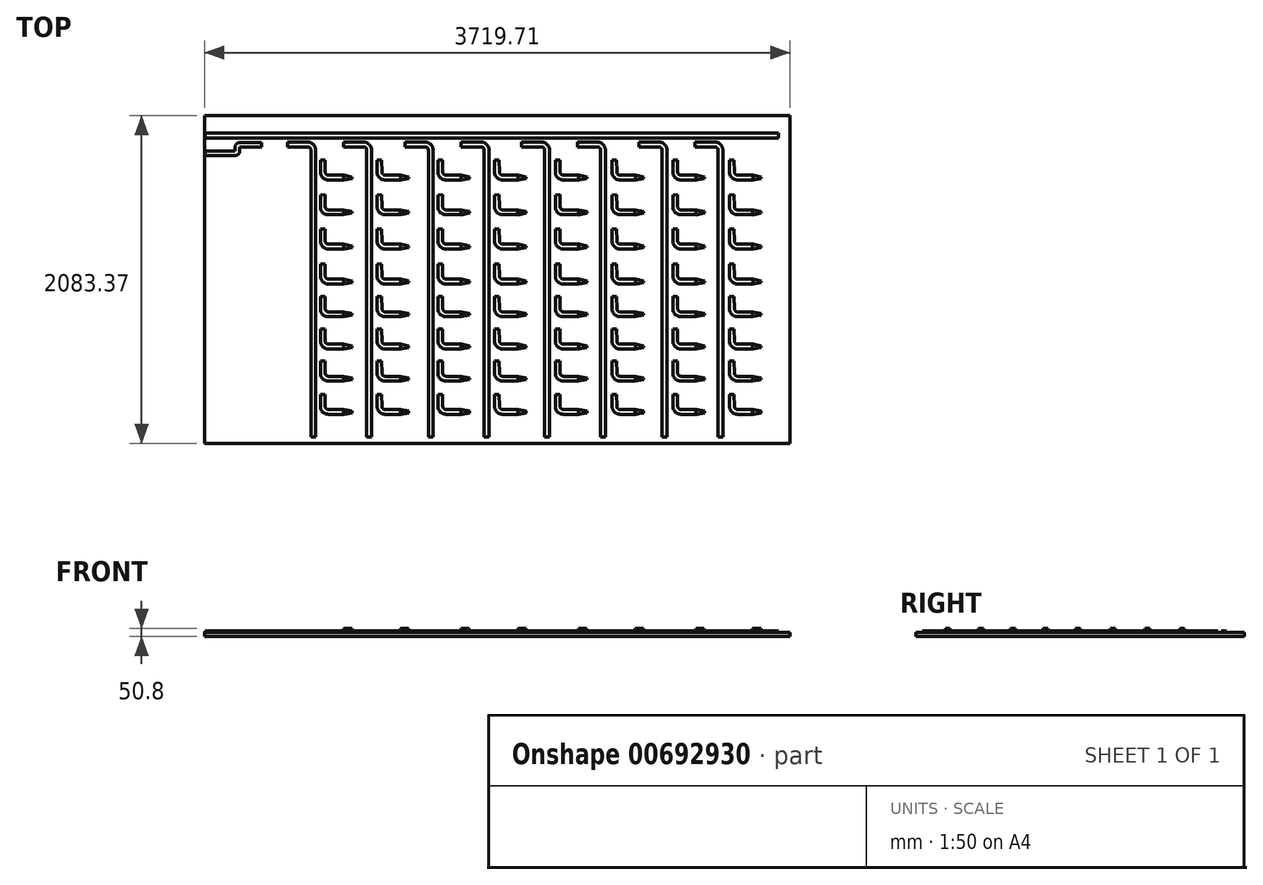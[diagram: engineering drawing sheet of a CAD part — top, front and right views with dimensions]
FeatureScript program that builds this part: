
annotation { "Feature Type Name" : "Feature", "Feature Type Description" : "" }
export const myFeature = defineFeature(function(context is Context, id is Id, definition is map)
    precondition{}
    {
        {
            var Q0;
            Q0=qCreatedBy(makeId("Top.planeOp"),FACE);
            var sketch = newSketch(context, id + "F0", { "sketchPlane" : qUnion([Q0])});
            skLineSegment(sketch, "E0.left", {"start": v(-935.56, 1469.09) * mm, "end": v(-935.56, -614.28) * mm});
            skPoint(sketch, "E0.middle", {"position": v(0, 0) * mm});
            skLineSegment(sketch, "E1", {"start": v(-935.56, 1469.09) * mm, "end": v(2784.15, 1469.09) * mm});
            skLineSegment(sketch, "E2", {"start": v(2784.15, 1469.09) * mm, "end": v(2784.15, -614.28) * mm});
            skLineSegment(sketch, "E3", {"start": v(2784.15, -614.28) * mm, "end": v(-935.56, -614.28) * mm});
            skSolve(sketch);
        }
        {
            var Q0;
            Q0=qSketchRegion(id+"F0",true);
            var Q1;
            Q1=makeQuery(id+"F0.imprint","IMPRINT",FACE,{"disambiguationData":[TD([[makeQuery(id+"F0.imprint","IMPRINT",EDGE,{"derivedFrom":sQuery(id+"F0.wireOp",EDGE,"E0.bottom")}),-1.0]])]});
            extrude(context, id + "F1", {"entities" : qUnion([Q0, Q1]), "oppositeDirection" : true, "depth" : 25.4 * mm, "offsetDistance" : 25.4 * mm});
        }
        {
            var Q0;
            Q0=makeQuery(id+"F1.opExtrude","CAP_FACE",FACE,{"disambiguationData":[OSD([sQuery(id+"F0.wireOp",EDGE,"E0.bottom"),sQuery(id+"F0.wireOp",EDGE,"E0.top"),sQuery(id+"F0.wireOp",EDGE,"E0.left"),sQuery(id+"F0.wireOp",EDGE,"E0.right")])],"isStart":true});
            var sketch = newSketch(context, id + "F2", { "sketchPlane" : qUnion([Q0])});
            skLineSegment(sketch, "E4", {"start": v(-51.41, 16.02) * mm, "end": v(0, 4.87) * mm});
            skLineSegment(sketch, "E5", {"start": v(0, 4.87) * mm, "end": v(0, -4.87) * mm});
            skLineSegment(sketch, "E6", {"start": v(0, -4.87) * mm, "end": v(-51.41, -14.6) * mm});
            skLineSegment(sketch, "E7", {"start": v(-51.41, 16.02) * mm, "end": v(-149.21, 16.02) * mm});
            skLineSegment(sketch, "E8", {"start": v(-149.21, -14.6) * mm, "end": v(-51.41, -14.6) * mm});
            skArc(sketch, "E9", {"start": v(-149.21, 16.02) * mm, "mid": v(-163.12, 21.71) * mm, "end": v(-169.05, 35.52) * mm});
            skArc(sketch, "E10", {"start": v(-149.21, -14.6) * mm, "mid": v(-184.84, 0.05) * mm, "end": v(-199.87, 35.52) * mm});
            skLineSegment(sketch, "E11", {"start": v(-169.05, 35.52) * mm, "end": v(-170.37, 112.54) * mm});
            skLineSegment(sketch, "E12", {"start": v(-170.37, 112.54) * mm, "end": v(-199.87, 112.03) * mm});
            skLineSegment(sketch, "E13", {"start": v(-199.87, 112.03) * mm, "end": v(-199.87, 35.52) * mm});
            skLineSegment(sketch, "E14", {"start": v(-51.41, 221.54) * mm, "end": v(0, 210.39) * mm});
            skLineSegment(sketch, "E15", {"start": v(0, 210.39) * mm, "end": v(0, 200.65) * mm});
            skLineSegment(sketch, "E16", {"start": v(0, 200.65) * mm, "end": v(-51.41, 190.92) * mm});
            skLineSegment(sketch, "E17", {"start": v(-51.41, 221.54) * mm, "end": v(-149.21, 221.54) * mm});
            skLineSegment(sketch, "E18", {"start": v(-149.21, 190.92) * mm, "end": v(-51.41, 190.92) * mm});
            skArc(sketch, "E19", {"start": v(-149.21, 221.54) * mm, "mid": v(-163.12, 227.23) * mm, "end": v(-169.05, 241.04) * mm});
            skArc(sketch, "E20", {"start": v(-149.21, 190.92) * mm, "mid": v(-184.84, 205.56) * mm, "end": v(-199.87, 241.04) * mm});
            skLineSegment(sketch, "E21", {"start": v(-169.05, 241.04) * mm, "end": v(-170.37, 318.06) * mm});
            skLineSegment(sketch, "E22", {"start": v(-170.37, 318.06) * mm, "end": v(-199.87, 317.55) * mm});
            skLineSegment(sketch, "E23", {"start": v(-199.87, 317.55) * mm, "end": v(-199.87, 241.04) * mm});
            skLineSegment(sketch, "E24", {"start": v(-51.41, -187.5) * mm, "end": v(0, -198.65) * mm});
            skLineSegment(sketch, "E25", {"start": v(0, -198.65) * mm, "end": v(0, -208.39) * mm});
            skLineSegment(sketch, "E26", {"start": v(0, -208.39) * mm, "end": v(-51.41, -218.12) * mm});
            skLineSegment(sketch, "E27", {"start": v(-51.41, -187.5) * mm, "end": v(-149.21, -187.5) * mm});
            skLineSegment(sketch, "E28", {"start": v(-149.21, -218.12) * mm, "end": v(-51.41, -218.12) * mm});
            skArc(sketch, "E29", {"start": v(-149.21, -187.5) * mm, "mid": v(-163.12, -181.8) * mm, "end": v(-169.05, -168) * mm});
            skArc(sketch, "E30", {"start": v(-149.21, -218.12) * mm, "mid": v(-184.84, -203.48) * mm, "end": v(-199.87, -168) * mm});
            skLineSegment(sketch, "E31", {"start": v(-169.05, -168) * mm, "end": v(-170.37, -90.98) * mm});
            skLineSegment(sketch, "E32", {"start": v(-170.37, -90.98) * mm, "end": v(-199.87, -91.49) * mm});
            skLineSegment(sketch, "E33", {"start": v(-199.87, -91.49) * mm, "end": v(-199.87, -168) * mm});
            skLineSegment(sketch, "E34", {"start": v(-51.41, -398.32) * mm, "end": v(0, -409.47) * mm});
            skLineSegment(sketch, "E35", {"start": v(0, -409.47) * mm, "end": v(0, -419.2) * mm});
            skLineSegment(sketch, "E36", {"start": v(0, -419.2) * mm, "end": v(-51.41, -428.94) * mm});
            skLineSegment(sketch, "E37", {"start": v(-51.41, -398.32) * mm, "end": v(-149.21, -398.32) * mm});
            skLineSegment(sketch, "E38", {"start": v(-149.21, -428.94) * mm, "end": v(-51.41, -428.94) * mm});
            skArc(sketch, "E39", {"start": v(-149.21, -398.32) * mm, "mid": v(-163.12, -392.63) * mm, "end": v(-169.05, -378.82) * mm});
            skArc(sketch, "E40", {"start": v(-149.21, -428.94) * mm, "mid": v(-184.84, -414.3) * mm, "end": v(-199.87, -378.82) * mm});
            skLineSegment(sketch, "E41", {"start": v(-169.05, -378.82) * mm, "end": v(-170.37, -301.8) * mm});
            skLineSegment(sketch, "E42", {"start": v(-170.37, -301.8) * mm, "end": v(-199.87, -302.3) * mm});
            skLineSegment(sketch, "E43", {"start": v(-199.87, -302.3) * mm, "end": v(-199.87, -378.82) * mm});
            skLineSegment(sketch, "E44", {"start": v(-51.41, 429.24) * mm, "end": v(0, 418.08) * mm});
            skLineSegment(sketch, "E45", {"start": v(0, 418.08) * mm, "end": v(0, 408.35) * mm});
            skLineSegment(sketch, "E46", {"start": v(0, 408.35) * mm, "end": v(-51.41, 398.61) * mm});
            skLineSegment(sketch, "E47", {"start": v(-51.41, 429.24) * mm, "end": v(-149.21, 429.24) * mm});
            skLineSegment(sketch, "E48", {"start": v(-149.21, 398.61) * mm, "end": v(-51.41, 398.61) * mm});
            skArc(sketch, "E49", {"start": v(-149.21, 429.24) * mm, "mid": v(-163.12, 434.93) * mm, "end": v(-169.05, 448.73) * mm});
            skArc(sketch, "E50", {"start": v(-149.21, 398.61) * mm, "mid": v(-184.84, 413.26) * mm, "end": v(-199.87, 448.73) * mm});
            skLineSegment(sketch, "E51", {"start": v(-169.05, 448.73) * mm, "end": v(-170.37, 525.76) * mm});
            skLineSegment(sketch, "E52", {"start": v(-170.37, 525.76) * mm, "end": v(-199.87, 525.25) * mm});
            skLineSegment(sketch, "E53", {"start": v(-199.87, 525.25) * mm, "end": v(-199.87, 448.73) * mm});
            skLineSegment(sketch, "E54", {"start": v(-51.41, 651.7) * mm, "end": v(0, 640.54) * mm});
            skLineSegment(sketch, "E55", {"start": v(0, 640.54) * mm, "end": v(0, 630.8) * mm});
            skLineSegment(sketch, "E56", {"start": v(0, 630.8) * mm, "end": v(-51.41, 621.07) * mm});
            skLineSegment(sketch, "E57", {"start": v(-51.41, 651.7) * mm, "end": v(-149.21, 651.7) * mm});
            skLineSegment(sketch, "E58", {"start": v(-149.21, 621.07) * mm, "end": v(-51.41, 621.07) * mm});
            skArc(sketch, "E59", {"start": v(-149.21, 651.7) * mm, "mid": v(-163.12, 657.39) * mm, "end": v(-169.05, 671.2) * mm});
            skArc(sketch, "E60", {"start": v(-149.21, 621.07) * mm, "mid": v(-184.84, 635.72) * mm, "end": v(-199.87, 671.2) * mm});
            skLineSegment(sketch, "E61", {"start": v(-169.05, 671.2) * mm, "end": v(-170.37, 748.22) * mm});
            skLineSegment(sketch, "E62", {"start": v(-170.37, 748.22) * mm, "end": v(-199.87, 747.71) * mm});
            skLineSegment(sketch, "E63", {"start": v(-199.87, 747.71) * mm, "end": v(-199.87, 671.2) * mm});
            skLineSegment(sketch, "E64", {"start": v(-51.41, 869.02) * mm, "end": v(0, 857.87) * mm});
            skLineSegment(sketch, "E65", {"start": v(0, 857.87) * mm, "end": v(0, 848.13) * mm});
            skLineSegment(sketch, "E66", {"start": v(0, 848.13) * mm, "end": v(-51.41, 838.4) * mm});
            skLineSegment(sketch, "E67", {"start": v(-51.41, 869.02) * mm, "end": v(-149.21, 869.02) * mm});
            skLineSegment(sketch, "E68", {"start": v(-149.21, 838.4) * mm, "end": v(-51.41, 838.4) * mm});
            skArc(sketch, "E69", {"start": v(-149.21, 869.02) * mm, "mid": v(-163.12, 874.71) * mm, "end": v(-169.05, 888.52) * mm});
            skArc(sketch, "E70", {"start": v(-149.21, 838.4) * mm, "mid": v(-184.84, 853.05) * mm, "end": v(-199.87, 888.52) * mm});
            skLineSegment(sketch, "E71", {"start": v(-169.05, 888.52) * mm, "end": v(-170.37, 965.54) * mm});
            skLineSegment(sketch, "E72", {"start": v(-170.37, 965.54) * mm, "end": v(-199.87, 965.04) * mm});
            skLineSegment(sketch, "E73", {"start": v(-199.87, 965.04) * mm, "end": v(-199.87, 888.52) * mm});
            skLineSegment(sketch, "E74", {"start": v(-51.41, 1090.15) * mm, "end": v(0, 1079) * mm});
            skLineSegment(sketch, "E75", {"start": v(0, 1079) * mm, "end": v(0, 1069.26) * mm});
            skLineSegment(sketch, "E76", {"start": v(0, 1069.26) * mm, "end": v(-51.41, 1059.52) * mm});
            skLineSegment(sketch, "E77", {"start": v(-51.41, 1090.15) * mm, "end": v(-149.21, 1090.15) * mm});
            skLineSegment(sketch, "E78", {"start": v(-149.21, 1059.52) * mm, "end": v(-51.41, 1059.52) * mm});
            skArc(sketch, "E79", {"start": v(-149.21, 1090.15) * mm, "mid": v(-163.12, 1095.84) * mm, "end": v(-169.05, 1109.64) * mm});
            skArc(sketch, "E80", {"start": v(-149.21, 1059.52) * mm, "mid": v(-184.84, 1074.17) * mm, "end": v(-199.87, 1109.64) * mm});
            skLineSegment(sketch, "E81", {"start": v(-169.05, 1109.64) * mm, "end": v(-170.37, 1186.67) * mm});
            skLineSegment(sketch, "E82", {"start": v(-170.37, 1186.67) * mm, "end": v(-199.87, 1186.16) * mm});
            skLineSegment(sketch, "E83", {"start": v(-199.87, 1186.16) * mm, "end": v(-199.87, 1109.64) * mm});
            skLineSegment(sketch, "E84", {"start": v(308.62, 16.02) * mm, "end": v(360.03, 4.87) * mm});
            skLineSegment(sketch, "E85", {"start": v(360.03, 4.87) * mm, "end": v(360.03, -4.87) * mm});
            skLineSegment(sketch, "E86", {"start": v(360.03, -4.87) * mm, "end": v(308.62, -14.6) * mm});
            skLineSegment(sketch, "E87", {"start": v(308.62, 16.02) * mm, "end": v(210.82, 16.02) * mm});
            skLineSegment(sketch, "E88", {"start": v(210.82, -14.6) * mm, "end": v(308.62, -14.6) * mm});
            skArc(sketch, "E89", {"start": v(210.82, 16.02) * mm, "mid": v(196.91, 21.71) * mm, "end": v(190.99, 35.52) * mm});
            skArc(sketch, "E90", {"start": v(210.82, -14.6) * mm, "mid": v(175.19, 0.05) * mm, "end": v(160.16, 35.52) * mm});
            skLineSegment(sketch, "E91", {"start": v(190.99, 35.52) * mm, "end": v(189.66, 112.54) * mm});
            skLineSegment(sketch, "E92", {"start": v(189.66, 112.54) * mm, "end": v(160.16, 112.03) * mm});
            skLineSegment(sketch, "E93", {"start": v(160.16, 112.03) * mm, "end": v(160.16, 35.52) * mm});
            skLineSegment(sketch, "E94", {"start": v(308.62, 221.54) * mm, "end": v(360.03, 210.39) * mm});
            skLineSegment(sketch, "E95", {"start": v(360.03, 210.39) * mm, "end": v(360.03, 200.65) * mm});
            skLineSegment(sketch, "E96", {"start": v(360.03, 200.65) * mm, "end": v(308.62, 190.92) * mm});
            skLineSegment(sketch, "E97", {"start": v(308.62, 221.54) * mm, "end": v(210.82, 221.54) * mm});
            skLineSegment(sketch, "E98", {"start": v(210.82, 190.92) * mm, "end": v(308.62, 190.92) * mm});
            skArc(sketch, "E99", {"start": v(210.82, 221.54) * mm, "mid": v(196.91, 227.23) * mm, "end": v(190.99, 241.04) * mm});
            skArc(sketch, "E100", {"start": v(210.82, 190.92) * mm, "mid": v(175.19, 205.56) * mm, "end": v(160.16, 241.04) * mm});
            skLineSegment(sketch, "E101", {"start": v(190.99, 241.04) * mm, "end": v(189.66, 318.06) * mm});
            skLineSegment(sketch, "E102", {"start": v(189.66, 318.06) * mm, "end": v(160.16, 317.55) * mm});
            skLineSegment(sketch, "E103", {"start": v(160.16, 317.55) * mm, "end": v(160.16, 241.04) * mm});
            skLineSegment(sketch, "E104", {"start": v(308.62, -187.5) * mm, "end": v(360.03, -198.65) * mm});
            skLineSegment(sketch, "E105", {"start": v(360.03, -198.65) * mm, "end": v(360.03, -208.39) * mm});
            skLineSegment(sketch, "E106", {"start": v(360.03, -208.39) * mm, "end": v(308.62, -218.12) * mm});
            skLineSegment(sketch, "E107", {"start": v(308.62, -187.5) * mm, "end": v(210.82, -187.5) * mm});
            skLineSegment(sketch, "E108", {"start": v(210.82, -218.12) * mm, "end": v(308.62, -218.12) * mm});
            skArc(sketch, "E109", {"start": v(210.82, -187.5) * mm, "mid": v(196.91, -181.8) * mm, "end": v(190.99, -168) * mm});
            skArc(sketch, "E110", {"start": v(210.82, -218.12) * mm, "mid": v(175.19, -203.48) * mm, "end": v(160.16, -168) * mm});
            skLineSegment(sketch, "E111", {"start": v(190.99, -168) * mm, "end": v(189.66, -90.98) * mm});
            skLineSegment(sketch, "E112", {"start": v(189.66, -90.98) * mm, "end": v(160.16, -91.49) * mm});
            skLineSegment(sketch, "E113", {"start": v(160.16, -91.49) * mm, "end": v(160.16, -168) * mm});
            skLineSegment(sketch, "E114", {"start": v(308.62, -398.32) * mm, "end": v(360.03, -409.47) * mm});
            skLineSegment(sketch, "E115", {"start": v(360.03, -409.47) * mm, "end": v(360.03, -419.2) * mm});
            skLineSegment(sketch, "E116", {"start": v(360.03, -419.2) * mm, "end": v(308.62, -428.94) * mm});
            skLineSegment(sketch, "E117", {"start": v(308.62, -398.32) * mm, "end": v(210.82, -398.32) * mm});
            skLineSegment(sketch, "E118", {"start": v(210.82, -428.94) * mm, "end": v(308.62, -428.94) * mm});
            skArc(sketch, "E119", {"start": v(210.82, -398.32) * mm, "mid": v(196.91, -392.63) * mm, "end": v(190.99, -378.82) * mm});
            skArc(sketch, "E120", {"start": v(210.82, -428.94) * mm, "mid": v(175.19, -414.3) * mm, "end": v(160.16, -378.82) * mm});
            skLineSegment(sketch, "E121", {"start": v(190.99, -378.82) * mm, "end": v(189.66, -301.8) * mm});
            skLineSegment(sketch, "E122", {"start": v(189.66, -301.8) * mm, "end": v(160.16, -302.3) * mm});
            skLineSegment(sketch, "E123", {"start": v(160.16, -302.3) * mm, "end": v(160.16, -378.82) * mm});
            skLineSegment(sketch, "E124", {"start": v(308.62, 429.24) * mm, "end": v(360.03, 418.08) * mm});
            skLineSegment(sketch, "E125", {"start": v(360.03, 418.08) * mm, "end": v(360.03, 408.35) * mm});
            skLineSegment(sketch, "E126", {"start": v(360.03, 408.35) * mm, "end": v(308.62, 398.61) * mm});
            skLineSegment(sketch, "E127", {"start": v(308.62, 429.24) * mm, "end": v(210.82, 429.24) * mm});
            skLineSegment(sketch, "E128", {"start": v(210.82, 398.61) * mm, "end": v(308.62, 398.61) * mm});
            skArc(sketch, "E129", {"start": v(210.82, 429.24) * mm, "mid": v(196.91, 434.93) * mm, "end": v(190.99, 448.73) * mm});
            skArc(sketch, "E130", {"start": v(210.82, 398.61) * mm, "mid": v(175.19, 413.26) * mm, "end": v(160.16, 448.73) * mm});
            skLineSegment(sketch, "E131", {"start": v(190.99, 448.73) * mm, "end": v(189.66, 525.76) * mm});
            skLineSegment(sketch, "E132", {"start": v(189.66, 525.76) * mm, "end": v(160.16, 525.25) * mm});
            skLineSegment(sketch, "E133", {"start": v(160.16, 525.25) * mm, "end": v(160.16, 448.73) * mm});
            skLineSegment(sketch, "E134", {"start": v(308.62, 651.7) * mm, "end": v(360.03, 640.54) * mm});
            skLineSegment(sketch, "E135", {"start": v(360.03, 640.54) * mm, "end": v(360.03, 630.8) * mm});
            skLineSegment(sketch, "E136", {"start": v(360.03, 630.8) * mm, "end": v(308.62, 621.07) * mm});
            skLineSegment(sketch, "E137", {"start": v(308.62, 651.7) * mm, "end": v(210.82, 651.7) * mm});
            skLineSegment(sketch, "E138", {"start": v(210.82, 621.07) * mm, "end": v(308.62, 621.07) * mm});
            skArc(sketch, "E139", {"start": v(210.82, 651.7) * mm, "mid": v(196.91, 657.39) * mm, "end": v(190.99, 671.2) * mm});
            skArc(sketch, "E140", {"start": v(210.82, 621.07) * mm, "mid": v(175.19, 635.72) * mm, "end": v(160.16, 671.2) * mm});
            skLineSegment(sketch, "E141", {"start": v(190.99, 671.2) * mm, "end": v(189.66, 748.22) * mm});
            skLineSegment(sketch, "E142", {"start": v(189.66, 748.22) * mm, "end": v(160.16, 747.71) * mm});
            skLineSegment(sketch, "E143", {"start": v(160.16, 747.71) * mm, "end": v(160.16, 671.2) * mm});
            skLineSegment(sketch, "E144", {"start": v(308.62, 869.02) * mm, "end": v(360.03, 857.87) * mm});
            skLineSegment(sketch, "E145", {"start": v(360.03, 857.87) * mm, "end": v(360.03, 848.13) * mm});
            skLineSegment(sketch, "E146", {"start": v(360.03, 848.13) * mm, "end": v(308.62, 838.4) * mm});
            skLineSegment(sketch, "E147", {"start": v(308.62, 869.02) * mm, "end": v(210.82, 869.02) * mm});
            skLineSegment(sketch, "E148", {"start": v(210.82, 838.4) * mm, "end": v(308.62, 838.4) * mm});
            skArc(sketch, "E149", {"start": v(210.82, 869.02) * mm, "mid": v(196.91, 874.71) * mm, "end": v(190.99, 888.52) * mm});
            skArc(sketch, "E150", {"start": v(210.82, 838.4) * mm, "mid": v(175.19, 853.05) * mm, "end": v(160.16, 888.52) * mm});
            skLineSegment(sketch, "E151", {"start": v(190.99, 888.52) * mm, "end": v(189.66, 965.54) * mm});
            skLineSegment(sketch, "E152", {"start": v(189.66, 965.54) * mm, "end": v(160.16, 965.04) * mm});
            skLineSegment(sketch, "E153", {"start": v(160.16, 965.04) * mm, "end": v(160.16, 888.52) * mm});
            skLineSegment(sketch, "E154", {"start": v(308.62, 1090.15) * mm, "end": v(360.03, 1079) * mm});
            skLineSegment(sketch, "E155", {"start": v(360.03, 1079) * mm, "end": v(360.03, 1069.26) * mm});
            skLineSegment(sketch, "E156", {"start": v(360.03, 1069.26) * mm, "end": v(308.62, 1059.52) * mm});
            skLineSegment(sketch, "E157", {"start": v(308.62, 1090.15) * mm, "end": v(210.82, 1090.15) * mm});
            skLineSegment(sketch, "E158", {"start": v(210.82, 1059.52) * mm, "end": v(308.62, 1059.52) * mm});
            skArc(sketch, "E159", {"start": v(210.82, 1090.15) * mm, "mid": v(196.91, 1095.84) * mm, "end": v(190.99, 1109.64) * mm});
            skArc(sketch, "E160", {"start": v(210.82, 1059.52) * mm, "mid": v(175.19, 1074.17) * mm, "end": v(160.16, 1109.64) * mm});
            skLineSegment(sketch, "E161", {"start": v(190.99, 1109.64) * mm, "end": v(189.66, 1186.67) * mm});
            skLineSegment(sketch, "E162", {"start": v(189.66, 1186.67) * mm, "end": v(160.16, 1186.16) * mm});
            skLineSegment(sketch, "E163", {"start": v(160.16, 1186.16) * mm, "end": v(160.16, 1109.64) * mm});
            skLineSegment(sketch, "E164", {"start": v(695.34, 16.02) * mm, "end": v(746.75, 4.87) * mm});
            skLineSegment(sketch, "E165", {"start": v(746.75, 4.87) * mm, "end": v(746.75, -4.87) * mm});
            skLineSegment(sketch, "E166", {"start": v(746.75, -4.87) * mm, "end": v(695.34, -14.6) * mm});
            skLineSegment(sketch, "E167", {"start": v(695.34, 16.02) * mm, "end": v(597.54, 16.02) * mm});
            skLineSegment(sketch, "E168", {"start": v(597.54, -14.6) * mm, "end": v(695.34, -14.6) * mm});
            skArc(sketch, "E169", {"start": v(597.54, 16.02) * mm, "mid": v(583.63, 21.71) * mm, "end": v(577.7, 35.52) * mm});
            skArc(sketch, "E170", {"start": v(597.54, -14.6) * mm, "mid": v(561.9, 0.05) * mm, "end": v(546.88, 35.52) * mm});
            skLineSegment(sketch, "E171", {"start": v(577.7, 35.52) * mm, "end": v(576.38, 112.54) * mm});
            skLineSegment(sketch, "E172", {"start": v(576.38, 112.54) * mm, "end": v(546.88, 112.03) * mm});
            skLineSegment(sketch, "E173", {"start": v(546.88, 112.03) * mm, "end": v(546.88, 35.52) * mm});
            skLineSegment(sketch, "E174", {"start": v(695.34, 221.54) * mm, "end": v(746.75, 210.39) * mm});
            skLineSegment(sketch, "E175", {"start": v(746.75, 210.39) * mm, "end": v(746.75, 200.65) * mm});
            skLineSegment(sketch, "E176", {"start": v(746.75, 200.65) * mm, "end": v(695.34, 190.92) * mm});
            skLineSegment(sketch, "E177", {"start": v(695.34, 221.54) * mm, "end": v(597.54, 221.54) * mm});
            skLineSegment(sketch, "E178", {"start": v(597.54, 190.92) * mm, "end": v(695.34, 190.92) * mm});
            skArc(sketch, "E179", {"start": v(597.54, 221.54) * mm, "mid": v(583.63, 227.23) * mm, "end": v(577.7, 241.04) * mm});
            skArc(sketch, "E180", {"start": v(597.54, 190.92) * mm, "mid": v(561.9, 205.56) * mm, "end": v(546.88, 241.04) * mm});
            skLineSegment(sketch, "E181", {"start": v(577.7, 241.04) * mm, "end": v(576.38, 318.06) * mm});
            skLineSegment(sketch, "E182", {"start": v(576.38, 318.06) * mm, "end": v(546.88, 317.55) * mm});
            skLineSegment(sketch, "E183", {"start": v(546.88, 317.55) * mm, "end": v(546.88, 241.04) * mm});
            skLineSegment(sketch, "E184", {"start": v(695.34, -187.5) * mm, "end": v(746.75, -198.65) * mm});
            skLineSegment(sketch, "E185", {"start": v(746.75, -198.65) * mm, "end": v(746.75, -208.39) * mm});
            skLineSegment(sketch, "E186", {"start": v(746.75, -208.39) * mm, "end": v(695.34, -218.12) * mm});
            skLineSegment(sketch, "E187", {"start": v(695.34, -187.5) * mm, "end": v(597.54, -187.5) * mm});
            skLineSegment(sketch, "E188", {"start": v(597.54, -218.12) * mm, "end": v(695.34, -218.12) * mm});
            skArc(sketch, "E189", {"start": v(597.54, -187.5) * mm, "mid": v(583.63, -181.8) * mm, "end": v(577.7, -168) * mm});
            skArc(sketch, "E190", {"start": v(597.54, -218.12) * mm, "mid": v(561.9, -203.48) * mm, "end": v(546.88, -168) * mm});
            skLineSegment(sketch, "E191", {"start": v(577.7, -168) * mm, "end": v(576.38, -90.98) * mm});
            skLineSegment(sketch, "E192", {"start": v(576.38, -90.98) * mm, "end": v(546.88, -91.49) * mm});
            skLineSegment(sketch, "E193", {"start": v(546.88, -91.49) * mm, "end": v(546.88, -168) * mm});
            skLineSegment(sketch, "E194", {"start": v(695.34, -398.32) * mm, "end": v(746.75, -409.47) * mm});
            skLineSegment(sketch, "E195", {"start": v(746.75, -409.47) * mm, "end": v(746.75, -419.2) * mm});
            skLineSegment(sketch, "E196", {"start": v(746.75, -419.2) * mm, "end": v(695.34, -428.94) * mm});
            skLineSegment(sketch, "E197", {"start": v(695.34, -398.32) * mm, "end": v(597.54, -398.32) * mm});
            skLineSegment(sketch, "E198", {"start": v(597.54, -428.94) * mm, "end": v(695.34, -428.94) * mm});
            skArc(sketch, "E199", {"start": v(597.54, -398.32) * mm, "mid": v(583.63, -392.63) * mm, "end": v(577.7, -378.82) * mm});
            skArc(sketch, "E200", {"start": v(597.54, -428.94) * mm, "mid": v(561.9, -414.3) * mm, "end": v(546.88, -378.82) * mm});
            skLineSegment(sketch, "E201", {"start": v(577.7, -378.82) * mm, "end": v(576.38, -301.8) * mm});
            skLineSegment(sketch, "E202", {"start": v(576.38, -301.8) * mm, "end": v(546.88, -302.3) * mm});
            skLineSegment(sketch, "E203", {"start": v(546.88, -302.3) * mm, "end": v(546.88, -378.82) * mm});
            skLineSegment(sketch, "E204", {"start": v(695.34, 429.24) * mm, "end": v(746.75, 418.08) * mm});
            skLineSegment(sketch, "E205", {"start": v(746.75, 418.08) * mm, "end": v(746.75, 408.35) * mm});
            skLineSegment(sketch, "E206", {"start": v(746.75, 408.35) * mm, "end": v(695.34, 398.61) * mm});
            skLineSegment(sketch, "E207", {"start": v(695.34, 429.24) * mm, "end": v(597.54, 429.24) * mm});
            skLineSegment(sketch, "E208", {"start": v(597.54, 398.61) * mm, "end": v(695.34, 398.61) * mm});
            skArc(sketch, "E209", {"start": v(597.54, 429.24) * mm, "mid": v(583.63, 434.93) * mm, "end": v(577.7, 448.73) * mm});
            skArc(sketch, "E210", {"start": v(597.54, 398.61) * mm, "mid": v(561.9, 413.26) * mm, "end": v(546.88, 448.73) * mm});
            skLineSegment(sketch, "E211", {"start": v(577.7, 448.73) * mm, "end": v(576.38, 525.76) * mm});
            skLineSegment(sketch, "E212", {"start": v(576.38, 525.76) * mm, "end": v(546.88, 525.25) * mm});
            skLineSegment(sketch, "E213", {"start": v(546.88, 525.25) * mm, "end": v(546.88, 448.73) * mm});
            skLineSegment(sketch, "E214", {"start": v(695.34, 651.7) * mm, "end": v(746.75, 640.54) * mm});
            skLineSegment(sketch, "E215", {"start": v(746.75, 640.54) * mm, "end": v(746.75, 630.8) * mm});
            skLineSegment(sketch, "E216", {"start": v(746.75, 630.8) * mm, "end": v(695.34, 621.07) * mm});
            skLineSegment(sketch, "E217", {"start": v(695.34, 651.7) * mm, "end": v(597.54, 651.7) * mm});
            skLineSegment(sketch, "E218", {"start": v(597.54, 621.07) * mm, "end": v(695.34, 621.07) * mm});
            skArc(sketch, "E219", {"start": v(597.54, 651.7) * mm, "mid": v(583.63, 657.39) * mm, "end": v(577.7, 671.2) * mm});
            skArc(sketch, "E220", {"start": v(597.54, 621.07) * mm, "mid": v(561.9, 635.72) * mm, "end": v(546.88, 671.2) * mm});
            skLineSegment(sketch, "E221", {"start": v(577.7, 671.2) * mm, "end": v(576.38, 748.22) * mm});
            skLineSegment(sketch, "E222", {"start": v(576.38, 748.22) * mm, "end": v(546.88, 747.71) * mm});
            skLineSegment(sketch, "E223", {"start": v(546.88, 747.71) * mm, "end": v(546.88, 671.2) * mm});
            skLineSegment(sketch, "E224", {"start": v(695.34, 869.02) * mm, "end": v(746.75, 857.87) * mm});
            skLineSegment(sketch, "E225", {"start": v(746.75, 857.87) * mm, "end": v(746.75, 848.13) * mm});
            skLineSegment(sketch, "E226", {"start": v(746.75, 848.13) * mm, "end": v(695.34, 838.4) * mm});
            skLineSegment(sketch, "E227", {"start": v(695.34, 869.02) * mm, "end": v(597.54, 869.02) * mm});
            skLineSegment(sketch, "E228", {"start": v(597.54, 838.4) * mm, "end": v(695.34, 838.4) * mm});
            skArc(sketch, "E229", {"start": v(597.54, 869.02) * mm, "mid": v(583.63, 874.71) * mm, "end": v(577.7, 888.52) * mm});
            skArc(sketch, "E230", {"start": v(597.54, 838.4) * mm, "mid": v(561.9, 853.05) * mm, "end": v(546.88, 888.52) * mm});
            skLineSegment(sketch, "E231", {"start": v(577.7, 888.52) * mm, "end": v(576.38, 965.54) * mm});
            skLineSegment(sketch, "E232", {"start": v(576.38, 965.54) * mm, "end": v(546.88, 965.04) * mm});
            skLineSegment(sketch, "E233", {"start": v(546.88, 965.04) * mm, "end": v(546.88, 888.52) * mm});
            skLineSegment(sketch, "E234", {"start": v(695.34, 1090.15) * mm, "end": v(746.75, 1079) * mm});
            skLineSegment(sketch, "E235", {"start": v(746.75, 1079) * mm, "end": v(746.75, 1069.26) * mm});
            skLineSegment(sketch, "E236", {"start": v(746.75, 1069.26) * mm, "end": v(695.34, 1059.52) * mm});
            skLineSegment(sketch, "E237", {"start": v(695.34, 1090.15) * mm, "end": v(597.54, 1090.15) * mm});
            skLineSegment(sketch, "E238", {"start": v(597.54, 1059.52) * mm, "end": v(695.34, 1059.52) * mm});
            skArc(sketch, "E239", {"start": v(597.54, 1090.15) * mm, "mid": v(583.63, 1095.84) * mm, "end": v(577.7, 1109.64) * mm});
            skArc(sketch, "E240", {"start": v(597.54, 1059.52) * mm, "mid": v(561.9, 1074.17) * mm, "end": v(546.88, 1109.64) * mm});
            skLineSegment(sketch, "E241", {"start": v(577.7, 1109.64) * mm, "end": v(576.38, 1186.67) * mm});
            skLineSegment(sketch, "E242", {"start": v(576.38, 1186.67) * mm, "end": v(546.88, 1186.16) * mm});
            skLineSegment(sketch, "E243", {"start": v(546.88, 1186.16) * mm, "end": v(546.88, 1109.64) * mm});
            skLineSegment(sketch, "E244", {"start": v(1055.37, 16.02) * mm, "end": v(1106.78, 4.87) * mm});
            skLineSegment(sketch, "E245", {"start": v(1106.78, 4.87) * mm, "end": v(1106.78, -4.87) * mm});
            skLineSegment(sketch, "E246", {"start": v(1106.78, -4.87) * mm, "end": v(1055.37, -14.6) * mm});
            skLineSegment(sketch, "E247", {"start": v(1055.37, 16.02) * mm, "end": v(957.57, 16.02) * mm});
            skLineSegment(sketch, "E248", {"start": v(957.57, -14.6) * mm, "end": v(1055.37, -14.6) * mm});
            skArc(sketch, "E249", {"start": v(957.57, 16.02) * mm, "mid": v(943.67, 21.71) * mm, "end": v(937.74, 35.52) * mm});
            skArc(sketch, "E250", {"start": v(957.57, -14.6) * mm, "mid": v(921.94, 0.05) * mm, "end": v(906.9, 35.52) * mm});
            skLineSegment(sketch, "E251", {"start": v(937.74, 35.52) * mm, "end": v(936.41, 112.54) * mm});
            skLineSegment(sketch, "E252", {"start": v(936.41, 112.54) * mm, "end": v(906.9, 112.03) * mm});
            skLineSegment(sketch, "E253", {"start": v(906.9, 112.03) * mm, "end": v(906.9, 35.52) * mm});
            skLineSegment(sketch, "E254", {"start": v(1055.37, 221.54) * mm, "end": v(1106.78, 210.39) * mm});
            skLineSegment(sketch, "E255", {"start": v(1106.78, 210.39) * mm, "end": v(1106.78, 200.65) * mm});
            skLineSegment(sketch, "E256", {"start": v(1106.78, 200.65) * mm, "end": v(1055.37, 190.92) * mm});
            skLineSegment(sketch, "E257", {"start": v(1055.37, 221.54) * mm, "end": v(957.57, 221.54) * mm});
            skLineSegment(sketch, "E258", {"start": v(957.57, 190.92) * mm, "end": v(1055.37, 190.92) * mm});
            skArc(sketch, "E259", {"start": v(957.57, 221.54) * mm, "mid": v(943.67, 227.23) * mm, "end": v(937.74, 241.04) * mm});
            skArc(sketch, "E260", {"start": v(957.57, 190.92) * mm, "mid": v(921.94, 205.56) * mm, "end": v(906.9, 241.04) * mm});
            skLineSegment(sketch, "E261", {"start": v(937.74, 241.04) * mm, "end": v(936.41, 318.06) * mm});
            skLineSegment(sketch, "E262", {"start": v(936.41, 318.06) * mm, "end": v(906.9, 317.55) * mm});
            skLineSegment(sketch, "E263", {"start": v(906.9, 317.55) * mm, "end": v(906.9, 241.04) * mm});
            skLineSegment(sketch, "E264", {"start": v(1055.37, -187.5) * mm, "end": v(1106.78, -198.65) * mm});
            skLineSegment(sketch, "E265", {"start": v(1106.78, -198.65) * mm, "end": v(1106.78, -208.39) * mm});
            skLineSegment(sketch, "E266", {"start": v(1106.78, -208.39) * mm, "end": v(1055.37, -218.12) * mm});
            skLineSegment(sketch, "E267", {"start": v(1055.37, -187.5) * mm, "end": v(957.57, -187.5) * mm});
            skLineSegment(sketch, "E268", {"start": v(957.57, -218.12) * mm, "end": v(1055.37, -218.12) * mm});
            skArc(sketch, "E269", {"start": v(957.57, -187.5) * mm, "mid": v(943.67, -181.8) * mm, "end": v(937.74, -168) * mm});
            skArc(sketch, "E270", {"start": v(957.57, -218.12) * mm, "mid": v(921.94, -203.48) * mm, "end": v(906.9, -168) * mm});
            skLineSegment(sketch, "E271", {"start": v(937.74, -168) * mm, "end": v(936.41, -90.98) * mm});
            skLineSegment(sketch, "E272", {"start": v(936.41, -90.98) * mm, "end": v(906.9, -91.49) * mm});
            skLineSegment(sketch, "E273", {"start": v(906.9, -91.49) * mm, "end": v(906.9, -168) * mm});
            skLineSegment(sketch, "E274", {"start": v(1055.37, -398.32) * mm, "end": v(1106.78, -409.47) * mm});
            skLineSegment(sketch, "E275", {"start": v(1106.78, -409.47) * mm, "end": v(1106.78, -419.2) * mm});
            skLineSegment(sketch, "E276", {"start": v(1106.78, -419.2) * mm, "end": v(1055.37, -428.94) * mm});
            skLineSegment(sketch, "E277", {"start": v(1055.37, -398.32) * mm, "end": v(957.57, -398.32) * mm});
            skLineSegment(sketch, "E278", {"start": v(957.57, -428.94) * mm, "end": v(1055.37, -428.94) * mm});
            skArc(sketch, "E279", {"start": v(957.57, -398.32) * mm, "mid": v(943.67, -392.63) * mm, "end": v(937.74, -378.82) * mm});
            skArc(sketch, "E280", {"start": v(957.57, -428.94) * mm, "mid": v(921.94, -414.3) * mm, "end": v(906.9, -378.82) * mm});
            skLineSegment(sketch, "E281", {"start": v(937.74, -378.82) * mm, "end": v(936.41, -301.8) * mm});
            skLineSegment(sketch, "E282", {"start": v(936.41, -301.8) * mm, "end": v(906.9, -302.3) * mm});
            skLineSegment(sketch, "E283", {"start": v(906.9, -302.3) * mm, "end": v(906.9, -378.82) * mm});
            skLineSegment(sketch, "E284", {"start": v(1055.37, 429.24) * mm, "end": v(1106.78, 418.08) * mm});
            skLineSegment(sketch, "E285", {"start": v(1106.78, 418.08) * mm, "end": v(1106.78, 408.35) * mm});
            skLineSegment(sketch, "E286", {"start": v(1106.78, 408.35) * mm, "end": v(1055.37, 398.61) * mm});
            skLineSegment(sketch, "E287", {"start": v(1055.37, 429.24) * mm, "end": v(957.57, 429.24) * mm});
            skLineSegment(sketch, "E288", {"start": v(957.57, 398.61) * mm, "end": v(1055.37, 398.61) * mm});
            skArc(sketch, "E289", {"start": v(957.57, 429.24) * mm, "mid": v(943.67, 434.93) * mm, "end": v(937.74, 448.73) * mm});
            skArc(sketch, "E290", {"start": v(957.57, 398.61) * mm, "mid": v(921.94, 413.26) * mm, "end": v(906.9, 448.73) * mm});
            skLineSegment(sketch, "E291", {"start": v(937.74, 448.73) * mm, "end": v(936.41, 525.76) * mm});
            skLineSegment(sketch, "E292", {"start": v(936.41, 525.76) * mm, "end": v(906.9, 525.25) * mm});
            skLineSegment(sketch, "E293", {"start": v(906.9, 525.25) * mm, "end": v(906.9, 448.73) * mm});
            skLineSegment(sketch, "E294", {"start": v(1055.37, 651.7) * mm, "end": v(1106.78, 640.54) * mm});
            skLineSegment(sketch, "E295", {"start": v(1106.78, 640.54) * mm, "end": v(1106.78, 630.8) * mm});
            skLineSegment(sketch, "E296", {"start": v(1106.78, 630.8) * mm, "end": v(1055.37, 621.07) * mm});
            skLineSegment(sketch, "E297", {"start": v(1055.37, 651.7) * mm, "end": v(957.57, 651.7) * mm});
            skLineSegment(sketch, "E298", {"start": v(957.57, 621.07) * mm, "end": v(1055.37, 621.07) * mm});
            skArc(sketch, "E299", {"start": v(957.57, 651.7) * mm, "mid": v(943.67, 657.39) * mm, "end": v(937.74, 671.2) * mm});
            skArc(sketch, "E300", {"start": v(957.57, 621.07) * mm, "mid": v(921.94, 635.72) * mm, "end": v(906.9, 671.2) * mm});
            skLineSegment(sketch, "E301", {"start": v(937.74, 671.2) * mm, "end": v(936.41, 748.22) * mm});
            skLineSegment(sketch, "E302", {"start": v(936.41, 748.22) * mm, "end": v(906.9, 747.71) * mm});
            skLineSegment(sketch, "E303", {"start": v(906.9, 747.71) * mm, "end": v(906.9, 671.2) * mm});
            skLineSegment(sketch, "E304", {"start": v(1055.37, 869.02) * mm, "end": v(1106.78, 857.87) * mm});
            skLineSegment(sketch, "E305", {"start": v(1106.78, 857.87) * mm, "end": v(1106.78, 848.13) * mm});
            skLineSegment(sketch, "E306", {"start": v(1106.78, 848.13) * mm, "end": v(1055.37, 838.4) * mm});
            skLineSegment(sketch, "E307", {"start": v(1055.37, 869.02) * mm, "end": v(957.57, 869.02) * mm});
            skLineSegment(sketch, "E308", {"start": v(957.57, 838.4) * mm, "end": v(1055.37, 838.4) * mm});
            skArc(sketch, "E309", {"start": v(957.57, 869.02) * mm, "mid": v(943.67, 874.71) * mm, "end": v(937.74, 888.52) * mm});
            skArc(sketch, "E310", {"start": v(957.57, 838.4) * mm, "mid": v(921.94, 853.05) * mm, "end": v(906.9, 888.52) * mm});
            skLineSegment(sketch, "E311", {"start": v(937.74, 888.52) * mm, "end": v(936.41, 965.54) * mm});
            skLineSegment(sketch, "E312", {"start": v(936.41, 965.54) * mm, "end": v(906.9, 965.04) * mm});
            skLineSegment(sketch, "E313", {"start": v(906.9, 965.04) * mm, "end": v(906.9, 888.52) * mm});
            skLineSegment(sketch, "E314", {"start": v(1055.37, 1090.15) * mm, "end": v(1106.78, 1079) * mm});
            skLineSegment(sketch, "E315", {"start": v(1106.78, 1079) * mm, "end": v(1106.78, 1069.26) * mm});
            skLineSegment(sketch, "E316", {"start": v(1106.78, 1069.26) * mm, "end": v(1055.37, 1059.52) * mm});
            skLineSegment(sketch, "E317", {"start": v(1055.37, 1090.15) * mm, "end": v(957.57, 1090.15) * mm});
            skLineSegment(sketch, "E318", {"start": v(957.57, 1059.52) * mm, "end": v(1055.37, 1059.52) * mm});
            skArc(sketch, "E319", {"start": v(957.57, 1090.15) * mm, "mid": v(943.67, 1095.84) * mm, "end": v(937.74, 1109.64) * mm});
            skArc(sketch, "E320", {"start": v(957.57, 1059.52) * mm, "mid": v(921.94, 1074.17) * mm, "end": v(906.9, 1109.64) * mm});
            skLineSegment(sketch, "E321", {"start": v(937.74, 1109.64) * mm, "end": v(936.41, 1186.67) * mm});
            skLineSegment(sketch, "E322", {"start": v(936.41, 1186.67) * mm, "end": v(906.9, 1186.16) * mm});
            skLineSegment(sketch, "E323", {"start": v(906.9, 1186.16) * mm, "end": v(906.9, 1109.64) * mm});
            skLineSegment(sketch, "E324", {"start": v(1440.8, 16.02) * mm, "end": v(1492.21, 4.87) * mm});
            skLineSegment(sketch, "E325", {"start": v(1492.21, 4.87) * mm, "end": v(1492.21, -4.87) * mm});
            skLineSegment(sketch, "E326", {"start": v(1492.21, -4.87) * mm, "end": v(1440.8, -14.6) * mm});
            skLineSegment(sketch, "E327", {"start": v(1440.8, 16.02) * mm, "end": v(1343, 16.02) * mm});
            skLineSegment(sketch, "E328", {"start": v(1343, -14.6) * mm, "end": v(1440.8, -14.6) * mm});
            skArc(sketch, "E329", {"start": v(1343, 16.02) * mm, "mid": v(1329.1, 21.71) * mm, "end": v(1323.17, 35.52) * mm});
            skArc(sketch, "E330", {"start": v(1343, -14.6) * mm, "mid": v(1307.37, 0.05) * mm, "end": v(1292.34, 35.52) * mm});
            skLineSegment(sketch, "E331", {"start": v(1323.17, 35.52) * mm, "end": v(1321.84, 112.54) * mm});
            skLineSegment(sketch, "E332", {"start": v(1321.84, 112.54) * mm, "end": v(1292.34, 112.03) * mm});
            skLineSegment(sketch, "E333", {"start": v(1292.34, 112.03) * mm, "end": v(1292.34, 35.52) * mm});
            skLineSegment(sketch, "E334", {"start": v(1440.8, 221.54) * mm, "end": v(1492.21, 210.39) * mm});
            skLineSegment(sketch, "E335", {"start": v(1492.21, 210.39) * mm, "end": v(1492.21, 200.65) * mm});
            skLineSegment(sketch, "E336", {"start": v(1492.21, 200.65) * mm, "end": v(1440.8, 190.92) * mm});
            skLineSegment(sketch, "E337", {"start": v(1440.8, 221.54) * mm, "end": v(1343, 221.54) * mm});
            skLineSegment(sketch, "E338", {"start": v(1343, 190.92) * mm, "end": v(1440.8, 190.92) * mm});
            skArc(sketch, "E339", {"start": v(1343, 221.54) * mm, "mid": v(1329.1, 227.23) * mm, "end": v(1323.17, 241.04) * mm});
            skArc(sketch, "E340", {"start": v(1343, 190.92) * mm, "mid": v(1307.37, 205.56) * mm, "end": v(1292.34, 241.04) * mm});
            skLineSegment(sketch, "E341", {"start": v(1323.17, 241.04) * mm, "end": v(1321.84, 318.06) * mm});
            skLineSegment(sketch, "E342", {"start": v(1321.84, 318.06) * mm, "end": v(1292.34, 317.55) * mm});
            skLineSegment(sketch, "E343", {"start": v(1292.34, 317.55) * mm, "end": v(1292.34, 241.04) * mm});
            skLineSegment(sketch, "E344", {"start": v(1440.8, -187.5) * mm, "end": v(1492.21, -198.65) * mm});
            skLineSegment(sketch, "E345", {"start": v(1492.21, -198.65) * mm, "end": v(1492.21, -208.39) * mm});
            skLineSegment(sketch, "E346", {"start": v(1492.21, -208.39) * mm, "end": v(1440.8, -218.12) * mm});
            skLineSegment(sketch, "E347", {"start": v(1440.8, -187.5) * mm, "end": v(1343, -187.5) * mm});
            skLineSegment(sketch, "E348", {"start": v(1343, -218.12) * mm, "end": v(1440.8, -218.12) * mm});
            skArc(sketch, "E349", {"start": v(1343, -187.5) * mm, "mid": v(1329.1, -181.8) * mm, "end": v(1323.17, -168) * mm});
            skArc(sketch, "E350", {"start": v(1343, -218.12) * mm, "mid": v(1307.37, -203.48) * mm, "end": v(1292.34, -168) * mm});
            skLineSegment(sketch, "E351", {"start": v(1323.17, -168) * mm, "end": v(1321.84, -90.98) * mm});
            skLineSegment(sketch, "E352", {"start": v(1321.84, -90.98) * mm, "end": v(1292.34, -91.49) * mm});
            skLineSegment(sketch, "E353", {"start": v(1292.34, -91.49) * mm, "end": v(1292.34, -168) * mm});
            skLineSegment(sketch, "E354", {"start": v(1440.8, -398.32) * mm, "end": v(1492.21, -409.47) * mm});
            skLineSegment(sketch, "E355", {"start": v(1492.21, -409.47) * mm, "end": v(1492.21, -419.2) * mm});
            skLineSegment(sketch, "E356", {"start": v(1492.21, -419.2) * mm, "end": v(1440.8, -428.94) * mm});
            skLineSegment(sketch, "E357", {"start": v(1440.8, -398.32) * mm, "end": v(1343, -398.32) * mm});
            skLineSegment(sketch, "E358", {"start": v(1343, -428.94) * mm, "end": v(1440.8, -428.94) * mm});
            skArc(sketch, "E359", {"start": v(1343, -398.32) * mm, "mid": v(1329.1, -392.63) * mm, "end": v(1323.17, -378.82) * mm});
            skArc(sketch, "E360", {"start": v(1343, -428.94) * mm, "mid": v(1307.37, -414.3) * mm, "end": v(1292.34, -378.82) * mm});
            skLineSegment(sketch, "E361", {"start": v(1323.17, -378.82) * mm, "end": v(1321.84, -301.8) * mm});
            skLineSegment(sketch, "E362", {"start": v(1321.84, -301.8) * mm, "end": v(1292.34, -302.3) * mm});
            skLineSegment(sketch, "E363", {"start": v(1292.34, -302.3) * mm, "end": v(1292.34, -378.82) * mm});
            skLineSegment(sketch, "E364", {"start": v(1440.8, 429.24) * mm, "end": v(1492.21, 418.08) * mm});
            skLineSegment(sketch, "E365", {"start": v(1492.21, 418.08) * mm, "end": v(1492.21, 408.35) * mm});
            skLineSegment(sketch, "E366", {"start": v(1492.21, 408.35) * mm, "end": v(1440.8, 398.61) * mm});
            skLineSegment(sketch, "E367", {"start": v(1440.8, 429.24) * mm, "end": v(1343, 429.24) * mm});
            skLineSegment(sketch, "E368", {"start": v(1343, 398.61) * mm, "end": v(1440.8, 398.61) * mm});
            skArc(sketch, "E369", {"start": v(1343, 429.24) * mm, "mid": v(1329.1, 434.93) * mm, "end": v(1323.17, 448.73) * mm});
            skArc(sketch, "E370", {"start": v(1343, 398.61) * mm, "mid": v(1307.37, 413.26) * mm, "end": v(1292.34, 448.73) * mm});
            skLineSegment(sketch, "E371", {"start": v(1323.17, 448.73) * mm, "end": v(1321.84, 525.76) * mm});
            skLineSegment(sketch, "E372", {"start": v(1321.84, 525.76) * mm, "end": v(1292.34, 525.25) * mm});
            skLineSegment(sketch, "E373", {"start": v(1292.34, 525.25) * mm, "end": v(1292.34, 448.73) * mm});
            skLineSegment(sketch, "E374", {"start": v(1440.8, 651.7) * mm, "end": v(1492.21, 640.54) * mm});
            skLineSegment(sketch, "E375", {"start": v(1492.21, 640.54) * mm, "end": v(1492.21, 630.8) * mm});
            skLineSegment(sketch, "E376", {"start": v(1492.21, 630.8) * mm, "end": v(1440.8, 621.07) * mm});
            skLineSegment(sketch, "E377", {"start": v(1440.8, 651.7) * mm, "end": v(1343, 651.7) * mm});
            skLineSegment(sketch, "E378", {"start": v(1343, 621.07) * mm, "end": v(1440.8, 621.07) * mm});
            skArc(sketch, "E379", {"start": v(1343, 651.7) * mm, "mid": v(1329.1, 657.39) * mm, "end": v(1323.17, 671.2) * mm});
            skArc(sketch, "E380", {"start": v(1343, 621.07) * mm, "mid": v(1307.37, 635.72) * mm, "end": v(1292.34, 671.2) * mm});
            skLineSegment(sketch, "E381", {"start": v(1323.17, 671.2) * mm, "end": v(1321.84, 748.22) * mm});
            skLineSegment(sketch, "E382", {"start": v(1321.84, 748.22) * mm, "end": v(1292.34, 747.71) * mm});
            skLineSegment(sketch, "E383", {"start": v(1292.34, 747.71) * mm, "end": v(1292.34, 671.2) * mm});
            skLineSegment(sketch, "E384", {"start": v(1440.8, 869.02) * mm, "end": v(1492.21, 857.87) * mm});
            skLineSegment(sketch, "E385", {"start": v(1492.21, 857.87) * mm, "end": v(1492.21, 848.13) * mm});
            skLineSegment(sketch, "E386", {"start": v(1492.21, 848.13) * mm, "end": v(1440.8, 838.4) * mm});
            skLineSegment(sketch, "E387", {"start": v(1440.8, 869.02) * mm, "end": v(1343, 869.02) * mm});
            skLineSegment(sketch, "E388", {"start": v(1343, 838.4) * mm, "end": v(1440.8, 838.4) * mm});
            skArc(sketch, "E389", {"start": v(1343, 869.02) * mm, "mid": v(1329.1, 874.71) * mm, "end": v(1323.17, 888.52) * mm});
            skArc(sketch, "E390", {"start": v(1343, 838.4) * mm, "mid": v(1307.37, 853.05) * mm, "end": v(1292.34, 888.52) * mm});
            skLineSegment(sketch, "E391", {"start": v(1323.17, 888.52) * mm, "end": v(1321.84, 965.54) * mm});
            skLineSegment(sketch, "E392", {"start": v(1321.84, 965.54) * mm, "end": v(1292.34, 965.04) * mm});
            skLineSegment(sketch, "E393", {"start": v(1292.34, 965.04) * mm, "end": v(1292.34, 888.52) * mm});
            skLineSegment(sketch, "E394", {"start": v(1440.8, 1090.15) * mm, "end": v(1492.21, 1079) * mm});
            skLineSegment(sketch, "E395", {"start": v(1492.21, 1079) * mm, "end": v(1492.21, 1069.26) * mm});
            skLineSegment(sketch, "E396", {"start": v(1492.21, 1069.26) * mm, "end": v(1440.8, 1059.52) * mm});
            skLineSegment(sketch, "E397", {"start": v(1440.8, 1090.15) * mm, "end": v(1343, 1090.15) * mm});
            skLineSegment(sketch, "E398", {"start": v(1343, 1059.52) * mm, "end": v(1440.8, 1059.52) * mm});
            skArc(sketch, "E399", {"start": v(1343, 1090.15) * mm, "mid": v(1329.1, 1095.84) * mm, "end": v(1323.17, 1109.64) * mm});
            skArc(sketch, "E400", {"start": v(1343, 1059.52) * mm, "mid": v(1307.37, 1074.17) * mm, "end": v(1292.34, 1109.64) * mm});
            skLineSegment(sketch, "E401", {"start": v(1323.17, 1109.64) * mm, "end": v(1321.84, 1186.67) * mm});
            skLineSegment(sketch, "E402", {"start": v(1321.84, 1186.67) * mm, "end": v(1292.34, 1186.16) * mm});
            skLineSegment(sketch, "E403", {"start": v(1292.34, 1186.16) * mm, "end": v(1292.34, 1109.64) * mm});
            skLineSegment(sketch, "E404", {"start": v(1800.83, 16.02) * mm, "end": v(1852.25, 4.87) * mm});
            skLineSegment(sketch, "E405", {"start": v(1852.25, 4.87) * mm, "end": v(1852.25, -4.87) * mm});
            skLineSegment(sketch, "E406", {"start": v(1852.25, -4.87) * mm, "end": v(1800.83, -14.6) * mm});
            skLineSegment(sketch, "E407", {"start": v(1800.83, 16.02) * mm, "end": v(1703.03, 16.02) * mm});
            skLineSegment(sketch, "E408", {"start": v(1703.03, -14.6) * mm, "end": v(1800.83, -14.6) * mm});
            skArc(sketch, "E409", {"start": v(1703.03, 16.02) * mm, "mid": v(1689.13, 21.71) * mm, "end": v(1683.2, 35.52) * mm});
            skArc(sketch, "E410", {"start": v(1703.03, -14.6) * mm, "mid": v(1667.4, 0.05) * mm, "end": v(1652.37, 35.52) * mm});
            skLineSegment(sketch, "E411", {"start": v(1683.2, 35.52) * mm, "end": v(1681.88, 112.54) * mm});
            skLineSegment(sketch, "E412", {"start": v(1681.88, 112.54) * mm, "end": v(1652.37, 112.03) * mm});
            skLineSegment(sketch, "E413", {"start": v(1652.37, 112.03) * mm, "end": v(1652.37, 35.52) * mm});
            skLineSegment(sketch, "E414", {"start": v(1800.83, 221.54) * mm, "end": v(1852.25, 210.39) * mm});
            skLineSegment(sketch, "E415", {"start": v(1852.25, 210.39) * mm, "end": v(1852.25, 200.65) * mm});
            skLineSegment(sketch, "E416", {"start": v(1852.25, 200.65) * mm, "end": v(1800.83, 190.92) * mm});
            skLineSegment(sketch, "E417", {"start": v(1800.83, 221.54) * mm, "end": v(1703.03, 221.54) * mm});
            skLineSegment(sketch, "E418", {"start": v(1703.03, 190.92) * mm, "end": v(1800.83, 190.92) * mm});
            skArc(sketch, "E419", {"start": v(1703.03, 221.54) * mm, "mid": v(1689.13, 227.23) * mm, "end": v(1683.2, 241.04) * mm});
            skArc(sketch, "E420", {"start": v(1703.03, 190.92) * mm, "mid": v(1667.4, 205.56) * mm, "end": v(1652.37, 241.04) * mm});
            skLineSegment(sketch, "E421", {"start": v(1683.2, 241.04) * mm, "end": v(1681.88, 318.06) * mm});
            skLineSegment(sketch, "E422", {"start": v(1681.88, 318.06) * mm, "end": v(1652.37, 317.55) * mm});
            skLineSegment(sketch, "E423", {"start": v(1652.37, 317.55) * mm, "end": v(1652.37, 241.04) * mm});
            skLineSegment(sketch, "E424", {"start": v(1800.83, -187.5) * mm, "end": v(1852.25, -198.65) * mm});
            skLineSegment(sketch, "E425", {"start": v(1852.25, -198.65) * mm, "end": v(1852.25, -208.39) * mm});
            skLineSegment(sketch, "E426", {"start": v(1852.25, -208.39) * mm, "end": v(1800.83, -218.12) * mm});
            skLineSegment(sketch, "E427", {"start": v(1800.83, -187.5) * mm, "end": v(1703.03, -187.5) * mm});
            skLineSegment(sketch, "E428", {"start": v(1703.03, -218.12) * mm, "end": v(1800.83, -218.12) * mm});
            skArc(sketch, "E429", {"start": v(1703.03, -187.5) * mm, "mid": v(1689.13, -181.8) * mm, "end": v(1683.2, -168) * mm});
            skArc(sketch, "E430", {"start": v(1703.03, -218.12) * mm, "mid": v(1667.4, -203.48) * mm, "end": v(1652.37, -168) * mm});
            skLineSegment(sketch, "E431", {"start": v(1683.2, -168) * mm, "end": v(1681.88, -90.98) * mm});
            skLineSegment(sketch, "E432", {"start": v(1681.88, -90.98) * mm, "end": v(1652.37, -91.49) * mm});
            skLineSegment(sketch, "E433", {"start": v(1652.37, -91.49) * mm, "end": v(1652.37, -168) * mm});
            skLineSegment(sketch, "E434", {"start": v(1800.83, -398.32) * mm, "end": v(1852.25, -409.47) * mm});
            skLineSegment(sketch, "E435", {"start": v(1852.25, -409.47) * mm, "end": v(1852.25, -419.2) * mm});
            skLineSegment(sketch, "E436", {"start": v(1852.25, -419.2) * mm, "end": v(1800.83, -428.94) * mm});
            skLineSegment(sketch, "E437", {"start": v(1800.83, -398.32) * mm, "end": v(1703.03, -398.32) * mm});
            skLineSegment(sketch, "E438", {"start": v(1703.03, -428.94) * mm, "end": v(1800.83, -428.94) * mm});
            skArc(sketch, "E439", {"start": v(1703.03, -398.32) * mm, "mid": v(1689.13, -392.63) * mm, "end": v(1683.2, -378.82) * mm});
            skArc(sketch, "E440", {"start": v(1703.03, -428.94) * mm, "mid": v(1667.4, -414.3) * mm, "end": v(1652.37, -378.82) * mm});
            skLineSegment(sketch, "E441", {"start": v(1683.2, -378.82) * mm, "end": v(1681.88, -301.8) * mm});
            skLineSegment(sketch, "E442", {"start": v(1681.88, -301.8) * mm, "end": v(1652.37, -302.3) * mm});
            skLineSegment(sketch, "E443", {"start": v(1652.37, -302.3) * mm, "end": v(1652.37, -378.82) * mm});
            skLineSegment(sketch, "E444", {"start": v(1800.83, 429.24) * mm, "end": v(1852.25, 418.08) * mm});
            skLineSegment(sketch, "E445", {"start": v(1852.25, 418.08) * mm, "end": v(1852.25, 408.35) * mm});
            skLineSegment(sketch, "E446", {"start": v(1852.25, 408.35) * mm, "end": v(1800.83, 398.61) * mm});
            skLineSegment(sketch, "E447", {"start": v(1800.83, 429.24) * mm, "end": v(1703.03, 429.24) * mm});
            skLineSegment(sketch, "E448", {"start": v(1703.03, 398.61) * mm, "end": v(1800.83, 398.61) * mm});
            skArc(sketch, "E449", {"start": v(1703.03, 429.24) * mm, "mid": v(1689.13, 434.93) * mm, "end": v(1683.2, 448.73) * mm});
            skArc(sketch, "E450", {"start": v(1703.03, 398.61) * mm, "mid": v(1667.4, 413.26) * mm, "end": v(1652.37, 448.73) * mm});
            skLineSegment(sketch, "E451", {"start": v(1683.2, 448.73) * mm, "end": v(1681.88, 525.76) * mm});
            skLineSegment(sketch, "E452", {"start": v(1681.88, 525.76) * mm, "end": v(1652.37, 525.25) * mm});
            skLineSegment(sketch, "E453", {"start": v(1652.37, 525.25) * mm, "end": v(1652.37, 448.73) * mm});
            skLineSegment(sketch, "E454", {"start": v(1800.83, 651.7) * mm, "end": v(1852.25, 640.54) * mm});
            skLineSegment(sketch, "E455", {"start": v(1852.25, 640.54) * mm, "end": v(1852.25, 630.8) * mm});
            skLineSegment(sketch, "E456", {"start": v(1852.25, 630.8) * mm, "end": v(1800.83, 621.07) * mm});
            skLineSegment(sketch, "E457", {"start": v(1800.83, 651.7) * mm, "end": v(1703.03, 651.7) * mm});
            skLineSegment(sketch, "E458", {"start": v(1703.03, 621.07) * mm, "end": v(1800.83, 621.07) * mm});
            skArc(sketch, "E459", {"start": v(1703.03, 651.7) * mm, "mid": v(1689.13, 657.39) * mm, "end": v(1683.2, 671.2) * mm});
            skArc(sketch, "E460", {"start": v(1703.03, 621.07) * mm, "mid": v(1667.4, 635.72) * mm, "end": v(1652.37, 671.2) * mm});
            skLineSegment(sketch, "E461", {"start": v(1683.2, 671.2) * mm, "end": v(1681.88, 748.22) * mm});
            skLineSegment(sketch, "E462", {"start": v(1681.88, 748.22) * mm, "end": v(1652.37, 747.71) * mm});
            skLineSegment(sketch, "E463", {"start": v(1652.37, 747.71) * mm, "end": v(1652.37, 671.2) * mm});
            skLineSegment(sketch, "E464", {"start": v(1800.83, 869.02) * mm, "end": v(1852.25, 857.87) * mm});
            skLineSegment(sketch, "E465", {"start": v(1852.25, 857.87) * mm, "end": v(1852.25, 848.13) * mm});
            skLineSegment(sketch, "E466", {"start": v(1852.25, 848.13) * mm, "end": v(1800.83, 838.4) * mm});
            skLineSegment(sketch, "E467", {"start": v(1800.83, 869.02) * mm, "end": v(1703.03, 869.02) * mm});
            skLineSegment(sketch, "E468", {"start": v(1703.03, 838.4) * mm, "end": v(1800.83, 838.4) * mm});
            skArc(sketch, "E469", {"start": v(1703.03, 869.02) * mm, "mid": v(1689.13, 874.71) * mm, "end": v(1683.2, 888.52) * mm});
            skArc(sketch, "E470", {"start": v(1703.03, 838.4) * mm, "mid": v(1667.4, 853.05) * mm, "end": v(1652.37, 888.52) * mm});
            skLineSegment(sketch, "E471", {"start": v(1683.2, 888.52) * mm, "end": v(1681.88, 965.54) * mm});
            skLineSegment(sketch, "E472", {"start": v(1681.88, 965.54) * mm, "end": v(1652.37, 965.04) * mm});
            skLineSegment(sketch, "E473", {"start": v(1652.37, 965.04) * mm, "end": v(1652.37, 888.52) * mm});
            skLineSegment(sketch, "E474", {"start": v(1800.83, 1090.15) * mm, "end": v(1852.25, 1079) * mm});
            skLineSegment(sketch, "E475", {"start": v(1852.25, 1079) * mm, "end": v(1852.25, 1069.26) * mm});
            skLineSegment(sketch, "E476", {"start": v(1852.25, 1069.26) * mm, "end": v(1800.83, 1059.52) * mm});
            skLineSegment(sketch, "E477", {"start": v(1800.83, 1090.15) * mm, "end": v(1703.03, 1090.15) * mm});
            skLineSegment(sketch, "E478", {"start": v(1703.03, 1059.52) * mm, "end": v(1800.83, 1059.52) * mm});
            skArc(sketch, "E479", {"start": v(1703.03, 1090.15) * mm, "mid": v(1689.13, 1095.84) * mm, "end": v(1683.2, 1109.64) * mm});
            skArc(sketch, "E480", {"start": v(1703.03, 1059.52) * mm, "mid": v(1667.4, 1074.17) * mm, "end": v(1652.37, 1109.64) * mm});
            skLineSegment(sketch, "E481", {"start": v(1683.2, 1109.64) * mm, "end": v(1681.88, 1186.67) * mm});
            skLineSegment(sketch, "E482", {"start": v(1681.88, 1186.67) * mm, "end": v(1652.37, 1186.16) * mm});
            skLineSegment(sketch, "E483", {"start": v(1652.37, 1186.16) * mm, "end": v(1652.37, 1109.64) * mm});
            skLineSegment(sketch, "E484", {"start": v(2187.55, 16.02) * mm, "end": v(2238.97, 4.87) * mm});
            skLineSegment(sketch, "E485", {"start": v(2238.97, 4.87) * mm, "end": v(2238.97, -4.87) * mm});
            skLineSegment(sketch, "E486", {"start": v(2238.97, -4.87) * mm, "end": v(2187.55, -14.6) * mm});
            skLineSegment(sketch, "E487", {"start": v(2187.55, 16.02) * mm, "end": v(2089.75, 16.02) * mm});
            skLineSegment(sketch, "E488", {"start": v(2089.75, -14.6) * mm, "end": v(2187.55, -14.6) * mm});
            skArc(sketch, "E489", {"start": v(2089.75, 16.02) * mm, "mid": v(2075.85, 21.71) * mm, "end": v(2069.92, 35.52) * mm});
            skArc(sketch, "E490", {"start": v(2089.75, -14.6) * mm, "mid": v(2054.12, 0.05) * mm, "end": v(2039.1, 35.52) * mm});
            skLineSegment(sketch, "E491", {"start": v(2069.92, 35.52) * mm, "end": v(2068.6, 112.54) * mm});
            skLineSegment(sketch, "E492", {"start": v(2068.6, 112.54) * mm, "end": v(2039.1, 112.03) * mm});
            skLineSegment(sketch, "E493", {"start": v(2039.1, 112.03) * mm, "end": v(2039.1, 35.52) * mm});
            skLineSegment(sketch, "E494", {"start": v(2187.55, 221.54) * mm, "end": v(2238.97, 210.39) * mm});
            skLineSegment(sketch, "E495", {"start": v(2238.97, 210.39) * mm, "end": v(2238.97, 200.65) * mm});
            skLineSegment(sketch, "E496", {"start": v(2238.97, 200.65) * mm, "end": v(2187.55, 190.92) * mm});
            skLineSegment(sketch, "E497", {"start": v(2187.55, 221.54) * mm, "end": v(2089.75, 221.54) * mm});
            skLineSegment(sketch, "E498", {"start": v(2089.75, 190.92) * mm, "end": v(2187.55, 190.92) * mm});
            skArc(sketch, "E499", {"start": v(2089.75, 221.54) * mm, "mid": v(2075.85, 227.23) * mm, "end": v(2069.92, 241.04) * mm});
            skArc(sketch, "E500", {"start": v(2089.75, 190.92) * mm, "mid": v(2054.12, 205.56) * mm, "end": v(2039.1, 241.04) * mm});
            skLineSegment(sketch, "E501", {"start": v(2069.92, 241.04) * mm, "end": v(2068.6, 318.06) * mm});
            skLineSegment(sketch, "E502", {"start": v(2068.6, 318.06) * mm, "end": v(2039.1, 317.55) * mm});
            skLineSegment(sketch, "E503", {"start": v(2039.1, 317.55) * mm, "end": v(2039.1, 241.04) * mm});
            skLineSegment(sketch, "E504", {"start": v(2187.55, -187.5) * mm, "end": v(2238.97, -198.65) * mm});
            skLineSegment(sketch, "E505", {"start": v(2238.97, -198.65) * mm, "end": v(2238.97, -208.39) * mm});
            skLineSegment(sketch, "E506", {"start": v(2238.97, -208.39) * mm, "end": v(2187.55, -218.12) * mm});
            skLineSegment(sketch, "E507", {"start": v(2187.55, -187.5) * mm, "end": v(2089.75, -187.5) * mm});
            skLineSegment(sketch, "E508", {"start": v(2089.75, -218.12) * mm, "end": v(2187.55, -218.12) * mm});
            skArc(sketch, "E509", {"start": v(2089.75, -187.5) * mm, "mid": v(2075.85, -181.8) * mm, "end": v(2069.92, -168) * mm});
            skArc(sketch, "E510", {"start": v(2089.75, -218.12) * mm, "mid": v(2054.12, -203.48) * mm, "end": v(2039.1, -168) * mm});
            skLineSegment(sketch, "E511", {"start": v(2069.92, -168) * mm, "end": v(2068.6, -90.98) * mm});
            skLineSegment(sketch, "E512", {"start": v(2068.6, -90.98) * mm, "end": v(2039.1, -91.49) * mm});
            skLineSegment(sketch, "E513", {"start": v(2039.1, -91.49) * mm, "end": v(2039.1, -168) * mm});
            skLineSegment(sketch, "E514", {"start": v(2187.55, -398.32) * mm, "end": v(2238.97, -409.47) * mm});
            skLineSegment(sketch, "E515", {"start": v(2238.97, -409.47) * mm, "end": v(2238.97, -419.2) * mm});
            skLineSegment(sketch, "E516", {"start": v(2238.97, -419.2) * mm, "end": v(2187.55, -428.94) * mm});
            skLineSegment(sketch, "E517", {"start": v(2187.55, -398.32) * mm, "end": v(2089.75, -398.32) * mm});
            skLineSegment(sketch, "E518", {"start": v(2089.75, -428.94) * mm, "end": v(2187.55, -428.94) * mm});
            skArc(sketch, "E519", {"start": v(2089.75, -398.32) * mm, "mid": v(2075.85, -392.63) * mm, "end": v(2069.92, -378.82) * mm});
            skArc(sketch, "E520", {"start": v(2089.75, -428.94) * mm, "mid": v(2054.12, -414.3) * mm, "end": v(2039.1, -378.82) * mm});
            skLineSegment(sketch, "E521", {"start": v(2069.92, -378.82) * mm, "end": v(2068.6, -301.8) * mm});
            skLineSegment(sketch, "E522", {"start": v(2068.6, -301.8) * mm, "end": v(2039.1, -302.3) * mm});
            skLineSegment(sketch, "E523", {"start": v(2039.1, -302.3) * mm, "end": v(2039.1, -378.82) * mm});
            skLineSegment(sketch, "E524", {"start": v(2187.55, 429.24) * mm, "end": v(2238.97, 418.08) * mm});
            skLineSegment(sketch, "E525", {"start": v(2238.97, 418.08) * mm, "end": v(2238.97, 408.35) * mm});
            skLineSegment(sketch, "E526", {"start": v(2238.97, 408.35) * mm, "end": v(2187.55, 398.61) * mm});
            skLineSegment(sketch, "E527", {"start": v(2187.55, 429.24) * mm, "end": v(2089.75, 429.24) * mm});
            skLineSegment(sketch, "E528", {"start": v(2089.75, 398.61) * mm, "end": v(2187.55, 398.61) * mm});
            skArc(sketch, "E529", {"start": v(2089.75, 429.24) * mm, "mid": v(2075.85, 434.93) * mm, "end": v(2069.92, 448.73) * mm});
            skArc(sketch, "E530", {"start": v(2089.75, 398.61) * mm, "mid": v(2054.12, 413.26) * mm, "end": v(2039.1, 448.73) * mm});
            skLineSegment(sketch, "E531", {"start": v(2069.92, 448.73) * mm, "end": v(2068.6, 525.76) * mm});
            skLineSegment(sketch, "E532", {"start": v(2068.6, 525.76) * mm, "end": v(2039.1, 525.25) * mm});
            skLineSegment(sketch, "E533", {"start": v(2039.1, 525.25) * mm, "end": v(2039.1, 448.73) * mm});
            skLineSegment(sketch, "E534", {"start": v(2187.55, 651.7) * mm, "end": v(2238.97, 640.54) * mm});
            skLineSegment(sketch, "E535", {"start": v(2238.97, 640.54) * mm, "end": v(2238.97, 630.8) * mm});
            skLineSegment(sketch, "E536", {"start": v(2238.97, 630.8) * mm, "end": v(2187.55, 621.07) * mm});
            skLineSegment(sketch, "E537", {"start": v(2187.55, 651.7) * mm, "end": v(2089.75, 651.7) * mm});
            skLineSegment(sketch, "E538", {"start": v(2089.75, 621.07) * mm, "end": v(2187.55, 621.07) * mm});
            skArc(sketch, "E539", {"start": v(2089.75, 651.7) * mm, "mid": v(2075.85, 657.39) * mm, "end": v(2069.92, 671.2) * mm});
            skArc(sketch, "E540", {"start": v(2089.75, 621.07) * mm, "mid": v(2054.12, 635.72) * mm, "end": v(2039.1, 671.2) * mm});
            skLineSegment(sketch, "E541", {"start": v(2069.92, 671.2) * mm, "end": v(2068.6, 748.22) * mm});
            skLineSegment(sketch, "E542", {"start": v(2068.6, 748.22) * mm, "end": v(2039.1, 747.71) * mm});
            skLineSegment(sketch, "E543", {"start": v(2039.1, 747.71) * mm, "end": v(2039.1, 671.2) * mm});
            skLineSegment(sketch, "E544", {"start": v(2187.55, 869.02) * mm, "end": v(2238.97, 857.87) * mm});
            skLineSegment(sketch, "E545", {"start": v(2238.97, 857.87) * mm, "end": v(2238.97, 848.13) * mm});
            skLineSegment(sketch, "E546", {"start": v(2238.97, 848.13) * mm, "end": v(2187.55, 838.4) * mm});
            skLineSegment(sketch, "E547", {"start": v(2187.55, 869.02) * mm, "end": v(2089.75, 869.02) * mm});
            skLineSegment(sketch, "E548", {"start": v(2089.75, 838.4) * mm, "end": v(2187.55, 838.4) * mm});
            skArc(sketch, "E549", {"start": v(2089.75, 869.02) * mm, "mid": v(2075.85, 874.71) * mm, "end": v(2069.92, 888.52) * mm});
            skArc(sketch, "E550", {"start": v(2089.75, 838.4) * mm, "mid": v(2054.12, 853.05) * mm, "end": v(2039.1, 888.52) * mm});
            skLineSegment(sketch, "E551", {"start": v(2069.92, 888.52) * mm, "end": v(2068.6, 965.54) * mm});
            skLineSegment(sketch, "E552", {"start": v(2068.6, 965.54) * mm, "end": v(2039.1, 965.04) * mm});
            skLineSegment(sketch, "E553", {"start": v(2039.1, 965.04) * mm, "end": v(2039.1, 888.52) * mm});
            skLineSegment(sketch, "E554", {"start": v(2187.55, 1090.15) * mm, "end": v(2238.97, 1079) * mm});
            skLineSegment(sketch, "E555", {"start": v(2238.97, 1079) * mm, "end": v(2238.97, 1069.26) * mm});
            skLineSegment(sketch, "E556", {"start": v(2238.97, 1069.26) * mm, "end": v(2187.55, 1059.52) * mm});
            skLineSegment(sketch, "E557", {"start": v(2187.55, 1090.15) * mm, "end": v(2089.75, 1090.15) * mm});
            skLineSegment(sketch, "E558", {"start": v(2089.75, 1059.52) * mm, "end": v(2187.55, 1059.52) * mm});
            skArc(sketch, "E559", {"start": v(2089.75, 1090.15) * mm, "mid": v(2075.85, 1095.84) * mm, "end": v(2069.92, 1109.64) * mm});
            skArc(sketch, "E560", {"start": v(2089.75, 1059.52) * mm, "mid": v(2054.12, 1074.17) * mm, "end": v(2039.1, 1109.64) * mm});
            skLineSegment(sketch, "E561", {"start": v(2069.92, 1109.64) * mm, "end": v(2068.6, 1186.67) * mm});
            skLineSegment(sketch, "E562", {"start": v(2068.6, 1186.67) * mm, "end": v(2039.1, 1186.16) * mm});
            skLineSegment(sketch, "E563", {"start": v(2039.1, 1186.16) * mm, "end": v(2039.1, 1109.64) * mm});
            skLineSegment(sketch, "E564", {"start": v(2547.58, 16.02) * mm, "end": v(2599, 4.87) * mm});
            skLineSegment(sketch, "E565", {"start": v(2599, 4.87) * mm, "end": v(2599, -4.87) * mm});
            skLineSegment(sketch, "E566", {"start": v(2599, -4.87) * mm, "end": v(2547.58, -14.6) * mm});
            skLineSegment(sketch, "E567", {"start": v(2547.58, 16.02) * mm, "end": v(2449.79, 16.02) * mm});
            skLineSegment(sketch, "E568", {"start": v(2449.79, -14.6) * mm, "end": v(2547.58, -14.6) * mm});
            skArc(sketch, "E569", {"start": v(2449.79, 16.02) * mm, "mid": v(2435.88, 21.71) * mm, "end": v(2429.95, 35.52) * mm});
            skArc(sketch, "E570", {"start": v(2449.79, -14.6) * mm, "mid": v(2414.15, 0.05) * mm, "end": v(2399.12, 35.52) * mm});
            skLineSegment(sketch, "E571", {"start": v(2429.95, 35.52) * mm, "end": v(2428.63, 112.54) * mm});
            skLineSegment(sketch, "E572", {"start": v(2428.63, 112.54) * mm, "end": v(2399.12, 112.03) * mm});
            skLineSegment(sketch, "E573", {"start": v(2399.12, 112.03) * mm, "end": v(2399.12, 35.52) * mm});
            skLineSegment(sketch, "E574", {"start": v(2547.58, 221.54) * mm, "end": v(2599, 210.39) * mm});
            skLineSegment(sketch, "E575", {"start": v(2599, 210.39) * mm, "end": v(2599, 200.65) * mm});
            skLineSegment(sketch, "E576", {"start": v(2599, 200.65) * mm, "end": v(2547.58, 190.92) * mm});
            skLineSegment(sketch, "E577", {"start": v(2547.58, 221.54) * mm, "end": v(2449.79, 221.54) * mm});
            skLineSegment(sketch, "E578", {"start": v(2449.79, 190.92) * mm, "end": v(2547.58, 190.92) * mm});
            skArc(sketch, "E579", {"start": v(2449.79, 221.54) * mm, "mid": v(2435.88, 227.23) * mm, "end": v(2429.95, 241.04) * mm});
            skArc(sketch, "E580", {"start": v(2449.79, 190.92) * mm, "mid": v(2414.15, 205.56) * mm, "end": v(2399.12, 241.04) * mm});
            skLineSegment(sketch, "E581", {"start": v(2429.95, 241.04) * mm, "end": v(2428.63, 318.06) * mm});
            skLineSegment(sketch, "E582", {"start": v(2428.63, 318.06) * mm, "end": v(2399.12, 317.55) * mm});
            skLineSegment(sketch, "E583", {"start": v(2399.12, 317.55) * mm, "end": v(2399.12, 241.04) * mm});
            skLineSegment(sketch, "E584", {"start": v(2547.58, -187.5) * mm, "end": v(2599, -198.65) * mm});
            skLineSegment(sketch, "E585", {"start": v(2599, -198.65) * mm, "end": v(2599, -208.39) * mm});
            skLineSegment(sketch, "E586", {"start": v(2599, -208.39) * mm, "end": v(2547.58, -218.12) * mm});
            skLineSegment(sketch, "E587", {"start": v(2547.58, -187.5) * mm, "end": v(2449.79, -187.5) * mm});
            skLineSegment(sketch, "E588", {"start": v(2449.79, -218.12) * mm, "end": v(2547.58, -218.12) * mm});
            skArc(sketch, "E589", {"start": v(2449.79, -187.5) * mm, "mid": v(2435.88, -181.8) * mm, "end": v(2429.95, -168) * mm});
            skArc(sketch, "E590", {"start": v(2449.79, -218.12) * mm, "mid": v(2414.15, -203.48) * mm, "end": v(2399.12, -168) * mm});
            skLineSegment(sketch, "E591", {"start": v(2429.95, -168) * mm, "end": v(2428.63, -90.98) * mm});
            skLineSegment(sketch, "E592", {"start": v(2428.63, -90.98) * mm, "end": v(2399.12, -91.49) * mm});
            skLineSegment(sketch, "E593", {"start": v(2399.12, -91.49) * mm, "end": v(2399.12, -168) * mm});
            skLineSegment(sketch, "E594", {"start": v(2547.58, -398.32) * mm, "end": v(2599, -409.47) * mm});
            skLineSegment(sketch, "E595", {"start": v(2599, -409.47) * mm, "end": v(2599, -419.2) * mm});
            skLineSegment(sketch, "E596", {"start": v(2599, -419.2) * mm, "end": v(2547.58, -428.94) * mm});
            skLineSegment(sketch, "E597", {"start": v(2547.58, -398.32) * mm, "end": v(2449.79, -398.32) * mm});
            skLineSegment(sketch, "E598", {"start": v(2449.79, -428.94) * mm, "end": v(2547.58, -428.94) * mm});
            skArc(sketch, "E599", {"start": v(2449.79, -398.32) * mm, "mid": v(2435.88, -392.63) * mm, "end": v(2429.95, -378.82) * mm});
            skArc(sketch, "E600", {"start": v(2449.79, -428.94) * mm, "mid": v(2414.15, -414.3) * mm, "end": v(2399.12, -378.82) * mm});
            skLineSegment(sketch, "E601", {"start": v(2429.95, -378.82) * mm, "end": v(2428.63, -301.8) * mm});
            skLineSegment(sketch, "E602", {"start": v(2428.63, -301.8) * mm, "end": v(2399.12, -302.3) * mm});
            skLineSegment(sketch, "E603", {"start": v(2399.12, -302.3) * mm, "end": v(2399.12, -378.82) * mm});
            skLineSegment(sketch, "E604", {"start": v(2547.58, 429.24) * mm, "end": v(2599, 418.08) * mm});
            skLineSegment(sketch, "E605", {"start": v(2599, 418.08) * mm, "end": v(2599, 408.35) * mm});
            skLineSegment(sketch, "E606", {"start": v(2599, 408.35) * mm, "end": v(2547.58, 398.61) * mm});
            skLineSegment(sketch, "E607", {"start": v(2547.58, 429.24) * mm, "end": v(2449.79, 429.24) * mm});
            skLineSegment(sketch, "E608", {"start": v(2449.79, 398.61) * mm, "end": v(2547.58, 398.61) * mm});
            skArc(sketch, "E609", {"start": v(2449.79, 429.24) * mm, "mid": v(2435.88, 434.93) * mm, "end": v(2429.95, 448.73) * mm});
            skArc(sketch, "E610", {"start": v(2449.79, 398.61) * mm, "mid": v(2414.15, 413.26) * mm, "end": v(2399.12, 448.73) * mm});
            skLineSegment(sketch, "E611", {"start": v(2429.95, 448.73) * mm, "end": v(2428.63, 525.76) * mm});
            skLineSegment(sketch, "E612", {"start": v(2428.63, 525.76) * mm, "end": v(2399.12, 525.25) * mm});
            skLineSegment(sketch, "E613", {"start": v(2399.12, 525.25) * mm, "end": v(2399.12, 448.73) * mm});
            skLineSegment(sketch, "E614", {"start": v(2547.58, 651.7) * mm, "end": v(2599, 640.54) * mm});
            skLineSegment(sketch, "E615", {"start": v(2599, 640.54) * mm, "end": v(2599, 630.8) * mm});
            skLineSegment(sketch, "E616", {"start": v(2599, 630.8) * mm, "end": v(2547.58, 621.07) * mm});
            skLineSegment(sketch, "E617", {"start": v(2547.58, 651.7) * mm, "end": v(2449.79, 651.7) * mm});
            skLineSegment(sketch, "E618", {"start": v(2449.79, 621.07) * mm, "end": v(2547.58, 621.07) * mm});
            skArc(sketch, "E619", {"start": v(2449.79, 651.7) * mm, "mid": v(2435.88, 657.39) * mm, "end": v(2429.95, 671.2) * mm});
            skArc(sketch, "E620", {"start": v(2449.79, 621.07) * mm, "mid": v(2414.15, 635.72) * mm, "end": v(2399.12, 671.2) * mm});
            skLineSegment(sketch, "E621", {"start": v(2429.95, 671.2) * mm, "end": v(2428.63, 748.22) * mm});
            skLineSegment(sketch, "E622", {"start": v(2428.63, 748.22) * mm, "end": v(2399.12, 747.71) * mm});
            skLineSegment(sketch, "E623", {"start": v(2399.12, 747.71) * mm, "end": v(2399.12, 671.2) * mm});
            skLineSegment(sketch, "E624", {"start": v(2547.58, 869.02) * mm, "end": v(2599, 857.87) * mm});
            skLineSegment(sketch, "E625", {"start": v(2599, 857.87) * mm, "end": v(2599, 848.13) * mm});
            skLineSegment(sketch, "E626", {"start": v(2599, 848.13) * mm, "end": v(2547.58, 838.4) * mm});
            skLineSegment(sketch, "E627", {"start": v(2547.58, 869.02) * mm, "end": v(2449.79, 869.02) * mm});
            skLineSegment(sketch, "E628", {"start": v(2449.79, 838.4) * mm, "end": v(2547.58, 838.4) * mm});
            skArc(sketch, "E629", {"start": v(2449.79, 869.02) * mm, "mid": v(2435.88, 874.71) * mm, "end": v(2429.95, 888.52) * mm});
            skArc(sketch, "E630", {"start": v(2449.79, 838.4) * mm, "mid": v(2414.15, 853.05) * mm, "end": v(2399.12, 888.52) * mm});
            skLineSegment(sketch, "E631", {"start": v(2429.95, 888.52) * mm, "end": v(2428.63, 965.54) * mm});
            skLineSegment(sketch, "E632", {"start": v(2428.63, 965.54) * mm, "end": v(2399.12, 965.04) * mm});
            skLineSegment(sketch, "E633", {"start": v(2399.12, 965.04) * mm, "end": v(2399.12, 888.52) * mm});
            skLineSegment(sketch, "E634", {"start": v(2547.58, 1090.15) * mm, "end": v(2599, 1079) * mm});
            skLineSegment(sketch, "E635", {"start": v(2599, 1079) * mm, "end": v(2599, 1069.26) * mm});
            skLineSegment(sketch, "E636", {"start": v(2599, 1069.26) * mm, "end": v(2547.58, 1059.52) * mm});
            skLineSegment(sketch, "E637", {"start": v(2547.58, 1090.15) * mm, "end": v(2449.79, 1090.15) * mm});
            skLineSegment(sketch, "E638", {"start": v(2449.79, 1059.52) * mm, "end": v(2547.58, 1059.52) * mm});
            skArc(sketch, "E639", {"start": v(2449.79, 1090.15) * mm, "mid": v(2435.88, 1095.84) * mm, "end": v(2429.95, 1109.64) * mm});
            skArc(sketch, "E640", {"start": v(2449.79, 1059.52) * mm, "mid": v(2414.15, 1074.17) * mm, "end": v(2399.12, 1109.64) * mm});
            skLineSegment(sketch, "E641", {"start": v(2429.95, 1109.64) * mm, "end": v(2428.63, 1186.67) * mm});
            skLineSegment(sketch, "E642", {"start": v(2428.63, 1186.67) * mm, "end": v(2399.12, 1186.16) * mm});
            skLineSegment(sketch, "E643", {"start": v(2399.12, 1186.16) * mm, "end": v(2399.12, 1109.64) * mm});
            skSolve(sketch);
        }
        {
            var Q0;
            Q0=qSketchRegion(id+"F2",true);
            extrude(context, id + "F3", {"entities" : qUnion([Q0]), "depth" : 10.16 * mm, "offsetDistance" : 25.4 * mm});
        }
        {
            var Q0;
            Q0=makeQuery(id+"F3.opExtrude","CAP_FACE",FACE,{"disambiguationData":[OSD([sQuery(id+"F2.wireOp",EDGE,"E4"),sQuery(id+"F2.wireOp",EDGE,"E5"),sQuery(id+"F2.wireOp",EDGE,"E6"),sQuery(id+"F2.wireOp",EDGE,"E7"),sQuery(id+"F2.wireOp",EDGE,"JgvzJjwD-TXg6-fWbI-FKHk-LL5GRCbPJZjB"),sQuery(id+"F2.wireOp",EDGE,"E8")])],"isStart":false});
            var sketch = newSketch(context, id + "F4", { "sketchPlane" : qUnion([Q0])});
            skLineSegment(sketch, "E644", {"start": v(-51.41, 16.02) * mm, "end": v(0, 4.87) * mm});
            skLineSegment(sketch, "E645", {"start": v(0, 4.87) * mm, "end": v(0, -4.87) * mm});
            skLineSegment(sketch, "E646", {"start": v(0, -4.87) * mm, "end": v(-51.41, -14.6) * mm});
            skLineSegment(sketch, "E647", {"start": v(-51.41, -14.6) * mm, "end": v(-51.41, 16.02) * mm});
            skLineSegment(sketch, "E648", {"start": v(-51.41, -187.57) * mm, "end": v(-0.18, -198.68) * mm});
            skLineSegment(sketch, "E649", {"start": v(-0.18, -198.68) * mm, "end": v(-0.18, -208.36) * mm});
            skLineSegment(sketch, "E650", {"start": v(-0.18, -208.36) * mm, "end": v(-51.41, -218.18) * mm});
            skLineSegment(sketch, "E651", {"start": v(-51.41, -218.18) * mm, "end": v(-51.41, -187.57) * mm});
            skLineSegment(sketch, "E652", {"start": v(-51.46, -398.32) * mm, "end": v(-0.24, -409.45) * mm});
            skLineSegment(sketch, "E653", {"start": v(-0.24, -409.45) * mm, "end": v(-0.24, -418.83) * mm});
            skLineSegment(sketch, "E654", {"start": v(-0.24, -418.83) * mm, "end": v(-51.67, -428.97) * mm});
            skLineSegment(sketch, "E655", {"start": v(-51.67, -428.97) * mm, "end": v(-51.46, -398.32) * mm});
            skLineSegment(sketch, "E656", {"start": v(-51.41, 190.93) * mm, "end": v(-0.1, 200.7) * mm});
            skLineSegment(sketch, "E657", {"start": v(-0.1, 200.7) * mm, "end": v(-0.1, 210.4) * mm});
            skLineSegment(sketch, "E658", {"start": v(-0.1, 210.4) * mm, "end": v(-51.48, 221.6) * mm});
            skLineSegment(sketch, "E659", {"start": v(-51.48, 221.6) * mm, "end": v(-51.41, 190.93) * mm});
            skLineSegment(sketch, "E660", {"start": v(-51.41, 429.32) * mm, "end": v(-0.27, 418) * mm});
            skLineSegment(sketch, "E661", {"start": v(-0.27, 418) * mm, "end": v(-0.27, 408.62) * mm});
            skLineSegment(sketch, "E662", {"start": v(-0.27, 408.62) * mm, "end": v(-51.24, 398.7) * mm});
            skLineSegment(sketch, "E663", {"start": v(-51.24, 398.7) * mm, "end": v(-51.41, 429.32) * mm});
            skLineSegment(sketch, "E664", {"start": v(-51.58, 651.97) * mm, "end": v(-0.24, 640.51) * mm});
            skLineSegment(sketch, "E665", {"start": v(-0.24, 640.51) * mm, "end": v(-0.24, 630.99) * mm});
            skLineSegment(sketch, "E666", {"start": v(-0.24, 630.99) * mm, "end": v(-51.58, 621.02) * mm});
            skLineSegment(sketch, "E667", {"start": v(-51.58, 621.02) * mm, "end": v(-51.58, 651.97) * mm});
            skLineSegment(sketch, "E668", {"start": v(-51.93, 869.16) * mm, "end": v(-0.38, 857.9) * mm});
            skLineSegment(sketch, "E669", {"start": v(-0.38, 857.9) * mm, "end": v(-0.38, 848.27) * mm});
            skLineSegment(sketch, "E670", {"start": v(-0.38, 848.27) * mm, "end": v(-51.68, 838.25) * mm});
            skLineSegment(sketch, "E671", {"start": v(-51.68, 838.25) * mm, "end": v(-51.93, 869.16) * mm});
            skLineSegment(sketch, "E672", {"start": v(-51.4, 1090.34) * mm, "end": v(-0.23, 1079.1) * mm});
            skLineSegment(sketch, "E673", {"start": v(-0.23, 1079.1) * mm, "end": v(-0.23, 1069.4) * mm});
            skLineSegment(sketch, "E674", {"start": v(-51.39, 1059.55) * mm, "end": v(-0.23, 1069.4) * mm});
            skLineSegment(sketch, "E675", {"start": v(-51.4, 1090.34) * mm, "end": v(-51.39, 1059.55) * mm});
            skLineSegment(sketch, "E676", {"start": v(308.37, 16.02) * mm, "end": v(359.79, 4.87) * mm});
            skLineSegment(sketch, "E677", {"start": v(359.79, 4.87) * mm, "end": v(359.79, -4.87) * mm});
            skLineSegment(sketch, "E678", {"start": v(359.79, -4.87) * mm, "end": v(308.37, -14.6) * mm});
            skLineSegment(sketch, "E679", {"start": v(308.37, -14.6) * mm, "end": v(308.37, 16.02) * mm});
            skLineSegment(sketch, "E680", {"start": v(308.37, -187.57) * mm, "end": v(359.6, -198.68) * mm});
            skLineSegment(sketch, "E681", {"start": v(359.6, -198.68) * mm, "end": v(359.6, -208.36) * mm});
            skLineSegment(sketch, "E682", {"start": v(359.6, -208.36) * mm, "end": v(308.37, -218.18) * mm});
            skLineSegment(sketch, "E683", {"start": v(308.37, -218.18) * mm, "end": v(308.37, -187.57) * mm});
            skLineSegment(sketch, "E684", {"start": v(308.33, -398.32) * mm, "end": v(359.54, -409.45) * mm});
            skLineSegment(sketch, "E685", {"start": v(359.54, -409.45) * mm, "end": v(359.54, -418.83) * mm});
            skLineSegment(sketch, "E686", {"start": v(359.54, -418.83) * mm, "end": v(308.11, -428.97) * mm});
            skLineSegment(sketch, "E687", {"start": v(308.11, -428.97) * mm, "end": v(308.33, -398.32) * mm});
            skLineSegment(sketch, "E688", {"start": v(308.37, 190.93) * mm, "end": v(359.68, 200.7) * mm});
            skLineSegment(sketch, "E689", {"start": v(359.68, 200.7) * mm, "end": v(359.68, 210.4) * mm});
            skLineSegment(sketch, "E690", {"start": v(359.68, 210.4) * mm, "end": v(308.3, 221.6) * mm});
            skLineSegment(sketch, "E691", {"start": v(308.3, 221.6) * mm, "end": v(308.37, 190.93) * mm});
            skLineSegment(sketch, "E692", {"start": v(308.37, 429.32) * mm, "end": v(359.51, 418) * mm});
            skLineSegment(sketch, "E693", {"start": v(359.51, 418) * mm, "end": v(359.51, 408.62) * mm});
            skLineSegment(sketch, "E694", {"start": v(359.51, 408.62) * mm, "end": v(308.55, 398.7) * mm});
            skLineSegment(sketch, "E695", {"start": v(308.55, 398.7) * mm, "end": v(308.37, 429.32) * mm});
            skLineSegment(sketch, "E696", {"start": v(308.2, 651.97) * mm, "end": v(359.54, 640.51) * mm});
            skLineSegment(sketch, "E697", {"start": v(359.54, 640.51) * mm, "end": v(359.54, 630.99) * mm});
            skLineSegment(sketch, "E698", {"start": v(359.54, 630.99) * mm, "end": v(308.2, 621.02) * mm});
            skLineSegment(sketch, "E699", {"start": v(308.2, 621.02) * mm, "end": v(308.2, 651.97) * mm});
            skLineSegment(sketch, "E700", {"start": v(307.85, 869.16) * mm, "end": v(359.4, 857.9) * mm});
            skLineSegment(sketch, "E701", {"start": v(359.4, 857.9) * mm, "end": v(359.4, 848.27) * mm});
            skLineSegment(sketch, "E702", {"start": v(359.4, 848.27) * mm, "end": v(308.1, 838.25) * mm});
            skLineSegment(sketch, "E703", {"start": v(308.1, 838.25) * mm, "end": v(307.85, 869.16) * mm});
            skLineSegment(sketch, "E704", {"start": v(308.39, 1090.34) * mm, "end": v(359.56, 1079.1) * mm});
            skLineSegment(sketch, "E705", {"start": v(359.56, 1079.1) * mm, "end": v(359.56, 1069.4) * mm});
            skLineSegment(sketch, "E706", {"start": v(308.4, 1059.55) * mm, "end": v(359.56, 1069.4) * mm});
            skLineSegment(sketch, "E707", {"start": v(308.39, 1090.34) * mm, "end": v(308.4, 1059.55) * mm});
            skLineSegment(sketch, "E708", {"start": v(694.77, 16.02) * mm, "end": v(746.18, 4.87) * mm});
            skLineSegment(sketch, "E709", {"start": v(746.18, 4.87) * mm, "end": v(746.18, -4.87) * mm});
            skLineSegment(sketch, "E710", {"start": v(746.18, -4.87) * mm, "end": v(694.77, -14.6) * mm});
            skLineSegment(sketch, "E711", {"start": v(694.77, -14.6) * mm, "end": v(694.77, 16.02) * mm});
            skLineSegment(sketch, "E712", {"start": v(694.77, -187.57) * mm, "end": v(746, -198.68) * mm});
            skLineSegment(sketch, "E713", {"start": v(746, -198.68) * mm, "end": v(746, -208.36) * mm});
            skLineSegment(sketch, "E714", {"start": v(746, -208.36) * mm, "end": v(694.77, -218.18) * mm});
            skLineSegment(sketch, "E715", {"start": v(694.77, -218.18) * mm, "end": v(694.77, -187.57) * mm});
            skLineSegment(sketch, "E716", {"start": v(694.72, -398.32) * mm, "end": v(745.94, -409.45) * mm});
            skLineSegment(sketch, "E717", {"start": v(745.94, -409.45) * mm, "end": v(745.94, -418.83) * mm});
            skLineSegment(sketch, "E718", {"start": v(745.94, -418.83) * mm, "end": v(694.5, -428.97) * mm});
            skLineSegment(sketch, "E719", {"start": v(694.5, -428.97) * mm, "end": v(694.72, -398.32) * mm});
            skLineSegment(sketch, "E720", {"start": v(694.77, 190.93) * mm, "end": v(746.07, 200.7) * mm});
            skLineSegment(sketch, "E721", {"start": v(746.07, 200.7) * mm, "end": v(746.07, 210.4) * mm});
            skLineSegment(sketch, "E722", {"start": v(746.07, 210.4) * mm, "end": v(694.7, 221.6) * mm});
            skLineSegment(sketch, "E723", {"start": v(694.7, 221.6) * mm, "end": v(694.77, 190.93) * mm});
            skLineSegment(sketch, "E724", {"start": v(694.77, 429.32) * mm, "end": v(745.9, 418) * mm});
            skLineSegment(sketch, "E725", {"start": v(745.9, 418) * mm, "end": v(745.9, 408.62) * mm});
            skLineSegment(sketch, "E726", {"start": v(745.9, 408.62) * mm, "end": v(694.94, 398.7) * mm});
            skLineSegment(sketch, "E727", {"start": v(694.94, 398.7) * mm, "end": v(694.77, 429.32) * mm});
            skLineSegment(sketch, "E728", {"start": v(694.6, 651.97) * mm, "end": v(745.94, 640.51) * mm});
            skLineSegment(sketch, "E729", {"start": v(745.94, 640.51) * mm, "end": v(745.94, 630.99) * mm});
            skLineSegment(sketch, "E730", {"start": v(745.94, 630.99) * mm, "end": v(694.6, 621.02) * mm});
            skLineSegment(sketch, "E731", {"start": v(694.6, 621.02) * mm, "end": v(694.6, 651.97) * mm});
            skLineSegment(sketch, "E732", {"start": v(694.25, 869.16) * mm, "end": v(745.8, 857.9) * mm});
            skLineSegment(sketch, "E733", {"start": v(745.8, 857.9) * mm, "end": v(745.8, 848.27) * mm});
            skLineSegment(sketch, "E734", {"start": v(745.8, 848.27) * mm, "end": v(694.5, 838.25) * mm});
            skLineSegment(sketch, "E735", {"start": v(694.5, 838.25) * mm, "end": v(694.25, 869.16) * mm});
            skLineSegment(sketch, "E736", {"start": v(694.78, 1090.34) * mm, "end": v(745.95, 1079.1) * mm});
            skLineSegment(sketch, "E737", {"start": v(745.95, 1079.1) * mm, "end": v(745.95, 1069.4) * mm});
            skLineSegment(sketch, "E738", {"start": v(694.8, 1059.55) * mm, "end": v(745.95, 1069.4) * mm});
            skLineSegment(sketch, "E739", {"start": v(694.78, 1090.34) * mm, "end": v(694.8, 1059.55) * mm});
            skLineSegment(sketch, "E740", {"start": v(1054.55, 16.02) * mm, "end": v(1105.97, 4.87) * mm});
            skLineSegment(sketch, "E741", {"start": v(1105.97, 4.87) * mm, "end": v(1105.97, -4.87) * mm});
            skLineSegment(sketch, "E742", {"start": v(1105.97, -4.87) * mm, "end": v(1054.55, -14.6) * mm});
            skLineSegment(sketch, "E743", {"start": v(1054.55, -14.6) * mm, "end": v(1054.55, 16.02) * mm});
            skLineSegment(sketch, "E744", {"start": v(1054.55, -187.57) * mm, "end": v(1105.78, -198.68) * mm});
            skLineSegment(sketch, "E745", {"start": v(1105.78, -198.68) * mm, "end": v(1105.78, -208.36) * mm});
            skLineSegment(sketch, "E746", {"start": v(1105.78, -208.36) * mm, "end": v(1054.55, -218.18) * mm});
            skLineSegment(sketch, "E747", {"start": v(1054.55, -218.18) * mm, "end": v(1054.55, -187.57) * mm});
            skLineSegment(sketch, "E748", {"start": v(1054.5, -398.32) * mm, "end": v(1105.72, -409.45) * mm});
            skLineSegment(sketch, "E749", {"start": v(1105.72, -409.45) * mm, "end": v(1105.72, -418.83) * mm});
            skLineSegment(sketch, "E750", {"start": v(1105.72, -418.83) * mm, "end": v(1054.3, -428.97) * mm});
            skLineSegment(sketch, "E751", {"start": v(1054.3, -428.97) * mm, "end": v(1054.5, -398.32) * mm});
            skLineSegment(sketch, "E752", {"start": v(1054.55, 190.93) * mm, "end": v(1105.86, 200.7) * mm});
            skLineSegment(sketch, "E753", {"start": v(1105.86, 200.7) * mm, "end": v(1105.86, 210.4) * mm});
            skLineSegment(sketch, "E754", {"start": v(1105.86, 210.4) * mm, "end": v(1054.5, 221.6) * mm});
            skLineSegment(sketch, "E755", {"start": v(1054.5, 221.6) * mm, "end": v(1054.55, 190.93) * mm});
            skLineSegment(sketch, "E756", {"start": v(1054.55, 429.32) * mm, "end": v(1105.7, 418) * mm});
            skLineSegment(sketch, "E757", {"start": v(1105.7, 418) * mm, "end": v(1105.7, 408.62) * mm});
            skLineSegment(sketch, "E758", {"start": v(1105.7, 408.62) * mm, "end": v(1054.73, 398.7) * mm});
            skLineSegment(sketch, "E759", {"start": v(1054.73, 398.7) * mm, "end": v(1054.55, 429.32) * mm});
            skLineSegment(sketch, "E760", {"start": v(1054.39, 651.97) * mm, "end": v(1105.73, 640.51) * mm});
            skLineSegment(sketch, "E761", {"start": v(1105.73, 640.51) * mm, "end": v(1105.73, 630.99) * mm});
            skLineSegment(sketch, "E762", {"start": v(1105.73, 630.99) * mm, "end": v(1054.39, 621.02) * mm});
            skLineSegment(sketch, "E763", {"start": v(1054.39, 621.02) * mm, "end": v(1054.39, 651.97) * mm});
            skLineSegment(sketch, "E764", {"start": v(1054.03, 869.16) * mm, "end": v(1105.59, 857.9) * mm});
            skLineSegment(sketch, "E765", {"start": v(1105.59, 857.9) * mm, "end": v(1105.59, 848.27) * mm});
            skLineSegment(sketch, "E766", {"start": v(1105.59, 848.27) * mm, "end": v(1054.28, 838.25) * mm});
            skLineSegment(sketch, "E767", {"start": v(1054.28, 838.25) * mm, "end": v(1054.03, 869.16) * mm});
            skLineSegment(sketch, "E768", {"start": v(1054.57, 1090.34) * mm, "end": v(1105.74, 1079.1) * mm});
            skLineSegment(sketch, "E769", {"start": v(1105.74, 1079.1) * mm, "end": v(1105.74, 1069.4) * mm});
            skLineSegment(sketch, "E770", {"start": v(1054.58, 1059.55) * mm, "end": v(1105.74, 1069.4) * mm});
            skLineSegment(sketch, "E771", {"start": v(1054.57, 1090.34) * mm, "end": v(1054.58, 1059.55) * mm});
            skLineSegment(sketch, "E772", {"start": v(1440.4, 15.8) * mm, "end": v(1491.82, 4.64) * mm});
            skLineSegment(sketch, "E773", {"start": v(1491.82, 4.64) * mm, "end": v(1491.82, -5.1) * mm});
            skLineSegment(sketch, "E774", {"start": v(1491.82, -5.1) * mm, "end": v(1440.4, -14.83) * mm});
            skLineSegment(sketch, "E775", {"start": v(1440.4, -14.83) * mm, "end": v(1440.4, 15.8) * mm});
            skLineSegment(sketch, "E776", {"start": v(1440.4, -187.79) * mm, "end": v(1491.63, -198.9) * mm});
            skLineSegment(sketch, "E777", {"start": v(1491.63, -198.9) * mm, "end": v(1491.63, -208.58) * mm});
            skLineSegment(sketch, "E778", {"start": v(1491.63, -208.58) * mm, "end": v(1440.4, -218.4) * mm});
            skLineSegment(sketch, "E779", {"start": v(1440.4, -218.4) * mm, "end": v(1440.4, -187.79) * mm});
            skLineSegment(sketch, "E780", {"start": v(1440.36, -398.55) * mm, "end": v(1491.57, -409.67) * mm});
            skLineSegment(sketch, "E781", {"start": v(1491.57, -409.67) * mm, "end": v(1491.57, -419.05) * mm});
            skLineSegment(sketch, "E782", {"start": v(1491.57, -419.05) * mm, "end": v(1440.14, -429.19) * mm});
            skLineSegment(sketch, "E783", {"start": v(1440.14, -429.19) * mm, "end": v(1440.36, -398.55) * mm});
            skLineSegment(sketch, "E784", {"start": v(1440.4, 190.71) * mm, "end": v(1491.7, 200.47) * mm});
            skLineSegment(sketch, "E785", {"start": v(1491.7, 200.47) * mm, "end": v(1491.7, 210.17) * mm});
            skLineSegment(sketch, "E786", {"start": v(1491.7, 210.17) * mm, "end": v(1440.34, 221.37) * mm});
            skLineSegment(sketch, "E787", {"start": v(1440.34, 221.37) * mm, "end": v(1440.4, 190.71) * mm});
            skLineSegment(sketch, "E788", {"start": v(1440.4, 429.1) * mm, "end": v(1491.55, 417.77) * mm});
            skLineSegment(sketch, "E789", {"start": v(1491.55, 417.77) * mm, "end": v(1491.55, 408.4) * mm});
            skLineSegment(sketch, "E790", {"start": v(1491.55, 408.4) * mm, "end": v(1440.58, 398.48) * mm});
            skLineSegment(sketch, "E791", {"start": v(1440.58, 398.48) * mm, "end": v(1440.4, 429.1) * mm});
            skLineSegment(sketch, "E792", {"start": v(1440.24, 651.75) * mm, "end": v(1491.58, 640.29) * mm});
            skLineSegment(sketch, "E793", {"start": v(1491.58, 640.29) * mm, "end": v(1491.58, 630.76) * mm});
            skLineSegment(sketch, "E794", {"start": v(1491.58, 630.76) * mm, "end": v(1440.24, 620.8) * mm});
            skLineSegment(sketch, "E795", {"start": v(1440.24, 620.8) * mm, "end": v(1440.24, 651.75) * mm});
            skLineSegment(sketch, "E796", {"start": v(1439.88, 868.94) * mm, "end": v(1491.44, 857.68) * mm});
            skLineSegment(sketch, "E797", {"start": v(1491.44, 857.68) * mm, "end": v(1491.44, 848.04) * mm});
            skLineSegment(sketch, "E798", {"start": v(1491.44, 848.04) * mm, "end": v(1440.13, 838.03) * mm});
            skLineSegment(sketch, "E799", {"start": v(1440.13, 838.03) * mm, "end": v(1439.88, 868.94) * mm});
            skLineSegment(sketch, "E800", {"start": v(1440.42, 1090.12) * mm, "end": v(1491.6, 1078.88) * mm});
            skLineSegment(sketch, "E801", {"start": v(1491.6, 1078.88) * mm, "end": v(1491.6, 1069.18) * mm});
            skLineSegment(sketch, "E802", {"start": v(1440.43, 1059.32) * mm, "end": v(1491.6, 1069.18) * mm});
            skLineSegment(sketch, "E803", {"start": v(1440.42, 1090.12) * mm, "end": v(1440.43, 1059.32) * mm});
            skLineSegment(sketch, "E804", {"start": v(1800.19, 15.8) * mm, "end": v(1851.6, 4.64) * mm});
            skLineSegment(sketch, "E805", {"start": v(1851.6, 4.64) * mm, "end": v(1851.6, -5.1) * mm});
            skLineSegment(sketch, "E806", {"start": v(1851.6, -5.1) * mm, "end": v(1800.19, -14.83) * mm});
            skLineSegment(sketch, "E807", {"start": v(1800.19, -14.83) * mm, "end": v(1800.19, 15.8) * mm});
            skLineSegment(sketch, "E808", {"start": v(1800.19, -187.79) * mm, "end": v(1851.42, -198.9) * mm});
            skLineSegment(sketch, "E809", {"start": v(1851.42, -198.9) * mm, "end": v(1851.42, -208.58) * mm});
            skLineSegment(sketch, "E810", {"start": v(1851.42, -208.58) * mm, "end": v(1800.19, -218.4) * mm});
            skLineSegment(sketch, "E811", {"start": v(1800.19, -218.4) * mm, "end": v(1800.19, -187.79) * mm});
            skLineSegment(sketch, "E812", {"start": v(1800.14, -398.55) * mm, "end": v(1851.36, -409.67) * mm});
            skLineSegment(sketch, "E813", {"start": v(1851.36, -409.67) * mm, "end": v(1851.36, -419.05) * mm});
            skLineSegment(sketch, "E814", {"start": v(1851.36, -419.05) * mm, "end": v(1799.93, -429.19) * mm});
            skLineSegment(sketch, "E815", {"start": v(1799.93, -429.19) * mm, "end": v(1800.14, -398.55) * mm});
            skLineSegment(sketch, "E816", {"start": v(1800.19, 190.71) * mm, "end": v(1851.5, 200.47) * mm});
            skLineSegment(sketch, "E817", {"start": v(1851.5, 200.47) * mm, "end": v(1851.5, 210.17) * mm});
            skLineSegment(sketch, "E818", {"start": v(1851.5, 210.17) * mm, "end": v(1800.13, 221.37) * mm});
            skLineSegment(sketch, "E819", {"start": v(1800.13, 221.37) * mm, "end": v(1800.19, 190.71) * mm});
            skLineSegment(sketch, "E820", {"start": v(1800.19, 429.1) * mm, "end": v(1851.33, 417.77) * mm});
            skLineSegment(sketch, "E821", {"start": v(1851.33, 417.77) * mm, "end": v(1851.33, 408.4) * mm});
            skLineSegment(sketch, "E822", {"start": v(1851.33, 408.4) * mm, "end": v(1800.37, 398.48) * mm});
            skLineSegment(sketch, "E823", {"start": v(1800.37, 398.48) * mm, "end": v(1800.19, 429.1) * mm});
            skLineSegment(sketch, "E824", {"start": v(1800.02, 651.75) * mm, "end": v(1851.36, 640.29) * mm});
            skLineSegment(sketch, "E825", {"start": v(1851.36, 640.29) * mm, "end": v(1851.36, 630.76) * mm});
            skLineSegment(sketch, "E826", {"start": v(1851.36, 630.76) * mm, "end": v(1800.02, 620.8) * mm});
            skLineSegment(sketch, "E827", {"start": v(1800.02, 620.8) * mm, "end": v(1800.02, 651.75) * mm});
            skLineSegment(sketch, "E828", {"start": v(1799.67, 868.94) * mm, "end": v(1851.22, 857.68) * mm});
            skLineSegment(sketch, "E829", {"start": v(1851.22, 857.68) * mm, "end": v(1851.22, 848.04) * mm});
            skLineSegment(sketch, "E830", {"start": v(1851.22, 848.04) * mm, "end": v(1799.92, 838.03) * mm});
            skLineSegment(sketch, "E831", {"start": v(1799.92, 838.03) * mm, "end": v(1799.67, 868.94) * mm});
            skLineSegment(sketch, "E832", {"start": v(1800.2, 1090.12) * mm, "end": v(1851.38, 1078.88) * mm});
            skLineSegment(sketch, "E833", {"start": v(1851.38, 1078.88) * mm, "end": v(1851.38, 1069.18) * mm});
            skLineSegment(sketch, "E834", {"start": v(1800.21, 1059.32) * mm, "end": v(1851.38, 1069.18) * mm});
            skLineSegment(sketch, "E835", {"start": v(1800.2, 1090.12) * mm, "end": v(1800.21, 1059.32) * mm});
            skLineSegment(sketch, "E836", {"start": v(2186.58, 15.8) * mm, "end": v(2238, 4.64) * mm});
            skLineSegment(sketch, "E837", {"start": v(2238, 4.64) * mm, "end": v(2238, -5.1) * mm});
            skLineSegment(sketch, "E838", {"start": v(2238, -5.1) * mm, "end": v(2186.58, -14.83) * mm});
            skLineSegment(sketch, "E839", {"start": v(2186.58, -14.83) * mm, "end": v(2186.58, 15.8) * mm});
            skLineSegment(sketch, "E840", {"start": v(2186.58, -187.79) * mm, "end": v(2237.81, -198.9) * mm});
            skLineSegment(sketch, "E841", {"start": v(2237.81, -198.9) * mm, "end": v(2237.81, -208.58) * mm});
            skLineSegment(sketch, "E842", {"start": v(2237.81, -208.58) * mm, "end": v(2186.58, -218.4) * mm});
            skLineSegment(sketch, "E843", {"start": v(2186.58, -218.4) * mm, "end": v(2186.58, -187.79) * mm});
            skLineSegment(sketch, "E844", {"start": v(2186.54, -398.55) * mm, "end": v(2237.76, -409.67) * mm});
            skLineSegment(sketch, "E845", {"start": v(2237.76, -409.67) * mm, "end": v(2237.76, -419.05) * mm});
            skLineSegment(sketch, "E846", {"start": v(2237.76, -419.05) * mm, "end": v(2186.33, -429.19) * mm});
            skLineSegment(sketch, "E847", {"start": v(2186.33, -429.19) * mm, "end": v(2186.54, -398.55) * mm});
            skLineSegment(sketch, "E848", {"start": v(2186.58, 190.71) * mm, "end": v(2237.89, 200.47) * mm});
            skLineSegment(sketch, "E849", {"start": v(2237.89, 200.47) * mm, "end": v(2237.89, 210.17) * mm});
            skLineSegment(sketch, "E850", {"start": v(2237.89, 210.17) * mm, "end": v(2186.52, 221.37) * mm});
            skLineSegment(sketch, "E851", {"start": v(2186.52, 221.37) * mm, "end": v(2186.58, 190.71) * mm});
            skLineSegment(sketch, "E852", {"start": v(2186.58, 429.1) * mm, "end": v(2237.73, 417.77) * mm});
            skLineSegment(sketch, "E853", {"start": v(2237.73, 417.77) * mm, "end": v(2237.73, 408.4) * mm});
            skLineSegment(sketch, "E854", {"start": v(2237.73, 408.4) * mm, "end": v(2186.76, 398.48) * mm});
            skLineSegment(sketch, "E855", {"start": v(2186.76, 398.48) * mm, "end": v(2186.58, 429.1) * mm});
            skLineSegment(sketch, "E856", {"start": v(2186.42, 651.75) * mm, "end": v(2237.76, 640.29) * mm});
            skLineSegment(sketch, "E857", {"start": v(2237.76, 640.29) * mm, "end": v(2237.76, 630.76) * mm});
            skLineSegment(sketch, "E858", {"start": v(2237.76, 630.76) * mm, "end": v(2186.42, 620.8) * mm});
            skLineSegment(sketch, "E859", {"start": v(2186.42, 620.8) * mm, "end": v(2186.42, 651.75) * mm});
            skLineSegment(sketch, "E860", {"start": v(2186.06, 868.94) * mm, "end": v(2237.62, 857.68) * mm});
            skLineSegment(sketch, "E861", {"start": v(2237.62, 857.68) * mm, "end": v(2237.62, 848.04) * mm});
            skLineSegment(sketch, "E862", {"start": v(2237.62, 848.04) * mm, "end": v(2186.31, 838.03) * mm});
            skLineSegment(sketch, "E863", {"start": v(2186.31, 838.03) * mm, "end": v(2186.06, 868.94) * mm});
            skLineSegment(sketch, "E864", {"start": v(2186.6, 1090.12) * mm, "end": v(2237.77, 1078.88) * mm});
            skLineSegment(sketch, "E865", {"start": v(2237.77, 1078.88) * mm, "end": v(2237.77, 1069.18) * mm});
            skLineSegment(sketch, "E866", {"start": v(2186.6, 1059.32) * mm, "end": v(2237.77, 1069.18) * mm});
            skLineSegment(sketch, "E867", {"start": v(2186.6, 1090.12) * mm, "end": v(2186.6, 1059.32) * mm});
            skLineSegment(sketch, "E868", {"start": v(2546.37, 15.8) * mm, "end": v(2597.78, 4.64) * mm});
            skLineSegment(sketch, "E869", {"start": v(2597.78, 4.64) * mm, "end": v(2597.78, -5.1) * mm});
            skLineSegment(sketch, "E870", {"start": v(2597.78, -5.1) * mm, "end": v(2546.37, -14.83) * mm});
            skLineSegment(sketch, "E871", {"start": v(2546.37, -14.83) * mm, "end": v(2546.37, 15.8) * mm});
            skLineSegment(sketch, "E872", {"start": v(2546.37, -187.79) * mm, "end": v(2597.6, -198.9) * mm});
            skLineSegment(sketch, "E873", {"start": v(2597.6, -198.9) * mm, "end": v(2597.6, -208.58) * mm});
            skLineSegment(sketch, "E874", {"start": v(2597.6, -208.58) * mm, "end": v(2546.37, -218.4) * mm});
            skLineSegment(sketch, "E875", {"start": v(2546.37, -218.4) * mm, "end": v(2546.37, -187.79) * mm});
            skLineSegment(sketch, "E876", {"start": v(2546.32, -398.55) * mm, "end": v(2597.54, -409.67) * mm});
            skLineSegment(sketch, "E877", {"start": v(2597.54, -409.67) * mm, "end": v(2597.54, -419.05) * mm});
            skLineSegment(sketch, "E878", {"start": v(2597.54, -419.05) * mm, "end": v(2546.11, -429.19) * mm});
            skLineSegment(sketch, "E879", {"start": v(2546.11, -429.19) * mm, "end": v(2546.32, -398.55) * mm});
            skLineSegment(sketch, "E880", {"start": v(2546.37, 190.71) * mm, "end": v(2597.68, 200.47) * mm});
            skLineSegment(sketch, "E881", {"start": v(2597.68, 200.47) * mm, "end": v(2597.68, 210.17) * mm});
            skLineSegment(sketch, "E882", {"start": v(2597.68, 210.17) * mm, "end": v(2546.3, 221.37) * mm});
            skLineSegment(sketch, "E883", {"start": v(2546.3, 221.37) * mm, "end": v(2546.37, 190.71) * mm});
            skLineSegment(sketch, "E884", {"start": v(2546.37, 429.1) * mm, "end": v(2597.51, 417.77) * mm});
            skLineSegment(sketch, "E885", {"start": v(2597.51, 417.77) * mm, "end": v(2597.51, 408.4) * mm});
            skLineSegment(sketch, "E886", {"start": v(2597.51, 408.4) * mm, "end": v(2546.55, 398.48) * mm});
            skLineSegment(sketch, "E887", {"start": v(2546.55, 398.48) * mm, "end": v(2546.37, 429.1) * mm});
            skLineSegment(sketch, "E888", {"start": v(2546.2, 651.75) * mm, "end": v(2597.54, 640.29) * mm});
            skLineSegment(sketch, "E889", {"start": v(2597.54, 640.29) * mm, "end": v(2597.54, 630.76) * mm});
            skLineSegment(sketch, "E890", {"start": v(2597.54, 630.76) * mm, "end": v(2546.2, 620.8) * mm});
            skLineSegment(sketch, "E891", {"start": v(2546.2, 620.8) * mm, "end": v(2546.2, 651.75) * mm});
            skLineSegment(sketch, "E892", {"start": v(2545.85, 868.94) * mm, "end": v(2597.4, 857.68) * mm});
            skLineSegment(sketch, "E893", {"start": v(2597.4, 857.68) * mm, "end": v(2597.4, 848.04) * mm});
            skLineSegment(sketch, "E894", {"start": v(2597.4, 848.04) * mm, "end": v(2546.1, 838.03) * mm});
            skLineSegment(sketch, "E895", {"start": v(2546.1, 838.03) * mm, "end": v(2545.85, 868.94) * mm});
            skLineSegment(sketch, "E896", {"start": v(2546.39, 1090.12) * mm, "end": v(2597.56, 1078.88) * mm});
            skLineSegment(sketch, "E897", {"start": v(2597.56, 1078.88) * mm, "end": v(2597.56, 1069.18) * mm});
            skLineSegment(sketch, "E898", {"start": v(2546.4, 1059.32) * mm, "end": v(2597.56, 1069.18) * mm});
            skLineSegment(sketch, "E899", {"start": v(2546.39, 1090.12) * mm, "end": v(2546.4, 1059.32) * mm});
            skSolve(sketch);
        }
        {
            var Q0;
            Q0=qSketchRegion(id+"F4",true);
            extrude(context, id + "F5", {"entities" : qUnion([Q0]), "depth" : 7.62 * mm, "offsetDistance" : 25.4 * mm});
        }
        {
            var Q0;
            Q0=makeQuery(id+"F5.opExtrude","CAP_FACE",FACE,{"disambiguationData":[OSD([sQuery(id+"F4.wireOp",EDGE,"E644"),sQuery(id+"F4.wireOp",EDGE,"E645"),sQuery(id+"F4.wireOp",EDGE,"E646"),sQuery(id+"F4.wireOp",EDGE,"E647")])],"isStart":false});
            var sketch = newSketch(context, id + "F6", { "sketchPlane" : qUnion([Q0])});
            skLineSegment(sketch, "E900", {"start": v(-51.41, 16.02) * mm, "end": v(0, 4.87) * mm});
            skLineSegment(sketch, "E901", {"start": v(0, 4.87) * mm, "end": v(0, -4.87) * mm});
            skLineSegment(sketch, "E902", {"start": v(0, -4.87) * mm, "end": v(-51.41, -14.6) * mm});
            skLineSegment(sketch, "E903", {"start": v(-51.41, -14.6) * mm, "end": v(-51.41, 16.02) * mm});
            skLineSegment(sketch, "E904", {"start": v(-51.52, -398.25) * mm, "end": v(-51.52, -428.6) * mm});
            skLineSegment(sketch, "E905", {"start": v(-51.52, -398.25) * mm, "end": v(-0.18, -409.56) * mm});
            skLineSegment(sketch, "E906", {"start": v(-0.18, -409.56) * mm, "end": v(-0.18, -418.79) * mm});
            skLineSegment(sketch, "E907", {"start": v(-0.18, -418.79) * mm, "end": v(-51.52, -428.6) * mm});
            skLineSegment(sketch, "E908", {"start": v(-51.34, -187.52) * mm, "end": v(-0.23, -198.69) * mm});
            skLineSegment(sketch, "E909", {"start": v(-0.23, -198.69) * mm, "end": v(-0.23, -208.28) * mm});
            skLineSegment(sketch, "E910", {"start": v(-0.23, -208.28) * mm, "end": v(-51.42, -218.1) * mm});
            skLineSegment(sketch, "E911", {"start": v(-51.42, -218.1) * mm, "end": v(-51.34, -187.52) * mm});
            skLineSegment(sketch, "E912", {"start": v(-51.38, 221.63) * mm, "end": v(-0.12, 210.32) * mm});
            skLineSegment(sketch, "E913", {"start": v(-0.12, 210.32) * mm, "end": v(-0.12, 200.72) * mm});
            skLineSegment(sketch, "E914", {"start": v(-0.12, 200.72) * mm, "end": v(-51.46, 190.9) * mm});
            skLineSegment(sketch, "E915", {"start": v(-51.46, 190.9) * mm, "end": v(-51.38, 221.63) * mm});
            skLineSegment(sketch, "E916", {"start": v(-51.23, 429.4) * mm, "end": v(-0.26, 417.82) * mm});
            skLineSegment(sketch, "E917", {"start": v(-0.26, 417.82) * mm, "end": v(-0.26, 408.52) * mm});
            skLineSegment(sketch, "E918", {"start": v(-0.26, 408.52) * mm, "end": v(-51.23, 398.8) * mm});
            skLineSegment(sketch, "E919", {"start": v(-51.23, 398.8) * mm, "end": v(-51.23, 429.4) * mm});
            skLineSegment(sketch, "E920", {"start": v(-51.43, 651.93) * mm, "end": v(-0.16, 640.4) * mm});
            skLineSegment(sketch, "E921", {"start": v(-0.16, 640.4) * mm, "end": v(-0.16, 631.17) * mm});
            skLineSegment(sketch, "E922", {"start": v(-0.16, 631.17) * mm, "end": v(-51.43, 621.2) * mm});
            skLineSegment(sketch, "E923", {"start": v(-51.72, 869.28) * mm, "end": v(-0.05, 857.77) * mm});
            skLineSegment(sketch, "E924", {"start": v(-0.05, 857.77) * mm, "end": v(-0.05, 848.48) * mm});
            skLineSegment(sketch, "E925", {"start": v(-0.05, 848.48) * mm, "end": v(-51.72, 838.3) * mm});
            skLineSegment(sketch, "E926", {"start": v(-51.72, 838.3) * mm, "end": v(-51.72, 869.28) * mm});
            skLineSegment(sketch, "E927", {"start": v(-51.22, 1090.31) * mm, "end": v(-0.1, 1078.92) * mm});
            skLineSegment(sketch, "E928", {"start": v(-0.1, 1078.92) * mm, "end": v(-0.1, 1069.6) * mm});
            skLineSegment(sketch, "E929", {"start": v(-0.1, 1069.6) * mm, "end": v(-51.22, 1059.65) * mm});
            skLineSegment(sketch, "E930", {"start": v(-51.22, 1059.65) * mm, "end": v(-51.22, 1090.31) * mm});
            skLineSegment(sketch, "E931", {"start": v(-51.43, 651.93) * mm, "end": v(-51.43, 621.2) * mm});
            skLineSegment(sketch, "E932", {"start": v(308.65, 16.02) * mm, "end": v(360.06, 4.87) * mm});
            skLineSegment(sketch, "E933", {"start": v(360.06, 4.87) * mm, "end": v(360.06, -4.87) * mm});
            skLineSegment(sketch, "E934", {"start": v(360.06, -4.87) * mm, "end": v(308.65, -14.6) * mm});
            skLineSegment(sketch, "E935", {"start": v(308.65, -14.6) * mm, "end": v(308.65, 16.02) * mm});
            skLineSegment(sketch, "E936", {"start": v(308.55, -398.25) * mm, "end": v(308.55, -428.6) * mm});
            skLineSegment(sketch, "E937", {"start": v(308.55, -398.25) * mm, "end": v(359.89, -409.56) * mm});
            skLineSegment(sketch, "E938", {"start": v(359.89, -409.56) * mm, "end": v(359.89, -418.79) * mm});
            skLineSegment(sketch, "E939", {"start": v(359.89, -418.79) * mm, "end": v(308.55, -428.6) * mm});
            skLineSegment(sketch, "E940", {"start": v(308.72, -187.52) * mm, "end": v(359.84, -198.69) * mm});
            skLineSegment(sketch, "E941", {"start": v(359.84, -198.69) * mm, "end": v(359.84, -208.28) * mm});
            skLineSegment(sketch, "E942", {"start": v(359.84, -208.28) * mm, "end": v(308.65, -218.1) * mm});
            skLineSegment(sketch, "E943", {"start": v(308.65, -218.1) * mm, "end": v(308.72, -187.52) * mm});
            skLineSegment(sketch, "E944", {"start": v(308.68, 221.63) * mm, "end": v(359.94, 210.32) * mm});
            skLineSegment(sketch, "E945", {"start": v(359.94, 210.32) * mm, "end": v(359.94, 200.72) * mm});
            skLineSegment(sketch, "E946", {"start": v(359.94, 200.72) * mm, "end": v(308.6, 190.9) * mm});
            skLineSegment(sketch, "E947", {"start": v(308.6, 190.9) * mm, "end": v(308.68, 221.63) * mm});
            skLineSegment(sketch, "E948", {"start": v(308.83, 429.4) * mm, "end": v(359.8, 417.82) * mm});
            skLineSegment(sketch, "E949", {"start": v(359.8, 417.82) * mm, "end": v(359.8, 408.52) * mm});
            skLineSegment(sketch, "E950", {"start": v(359.8, 408.52) * mm, "end": v(308.83, 398.8) * mm});
            skLineSegment(sketch, "E951", {"start": v(308.83, 398.8) * mm, "end": v(308.83, 429.4) * mm});
            skLineSegment(sketch, "E952", {"start": v(308.63, 651.93) * mm, "end": v(359.9, 640.4) * mm});
            skLineSegment(sketch, "E953", {"start": v(359.9, 640.4) * mm, "end": v(359.9, 631.17) * mm});
            skLineSegment(sketch, "E954", {"start": v(359.9, 631.17) * mm, "end": v(308.63, 621.2) * mm});
            skLineSegment(sketch, "E955", {"start": v(308.34, 869.28) * mm, "end": v(360.02, 857.77) * mm});
            skLineSegment(sketch, "E956", {"start": v(360.02, 857.77) * mm, "end": v(360.02, 848.48) * mm});
            skLineSegment(sketch, "E957", {"start": v(360.02, 848.48) * mm, "end": v(308.34, 838.3) * mm});
            skLineSegment(sketch, "E958", {"start": v(308.34, 838.3) * mm, "end": v(308.34, 869.28) * mm});
            skLineSegment(sketch, "E959", {"start": v(308.85, 1090.31) * mm, "end": v(359.96, 1078.92) * mm});
            skLineSegment(sketch, "E960", {"start": v(359.96, 1078.92) * mm, "end": v(359.96, 1069.6) * mm});
            skLineSegment(sketch, "E961", {"start": v(359.96, 1069.6) * mm, "end": v(308.85, 1059.65) * mm});
            skLineSegment(sketch, "E962", {"start": v(308.85, 1059.65) * mm, "end": v(308.85, 1090.31) * mm});
            skLineSegment(sketch, "E963", {"start": v(308.63, 651.93) * mm, "end": v(308.63, 621.2) * mm});
            skLineSegment(sketch, "E964", {"start": v(694.53, 15.77) * mm, "end": v(745.94, 4.62) * mm});
            skLineSegment(sketch, "E965", {"start": v(745.94, 4.62) * mm, "end": v(745.94, -5.12) * mm});
            skLineSegment(sketch, "E966", {"start": v(745.94, -5.12) * mm, "end": v(694.53, -14.85) * mm});
            skLineSegment(sketch, "E967", {"start": v(694.53, -14.85) * mm, "end": v(694.53, 15.77) * mm});
            skLineSegment(sketch, "E968", {"start": v(694.43, -398.5) * mm, "end": v(694.43, -428.86) * mm});
            skLineSegment(sketch, "E969", {"start": v(694.43, -398.5) * mm, "end": v(745.76, -409.81) * mm});
            skLineSegment(sketch, "E970", {"start": v(745.76, -409.81) * mm, "end": v(745.76, -419.04) * mm});
            skLineSegment(sketch, "E971", {"start": v(745.76, -419.04) * mm, "end": v(694.43, -428.86) * mm});
            skLineSegment(sketch, "E972", {"start": v(694.6, -187.78) * mm, "end": v(745.72, -198.94) * mm});
            skLineSegment(sketch, "E973", {"start": v(745.72, -198.94) * mm, "end": v(745.72, -208.53) * mm});
            skLineSegment(sketch, "E974", {"start": v(745.72, -208.53) * mm, "end": v(694.52, -218.36) * mm});
            skLineSegment(sketch, "E975", {"start": v(694.52, -218.36) * mm, "end": v(694.6, -187.78) * mm});
            skLineSegment(sketch, "E976", {"start": v(694.56, 221.38) * mm, "end": v(745.82, 210.07) * mm});
            skLineSegment(sketch, "E977", {"start": v(745.82, 210.07) * mm, "end": v(745.82, 200.47) * mm});
            skLineSegment(sketch, "E978", {"start": v(745.82, 200.47) * mm, "end": v(694.48, 190.65) * mm});
            skLineSegment(sketch, "E979", {"start": v(694.48, 190.65) * mm, "end": v(694.56, 221.38) * mm});
            skLineSegment(sketch, "E980", {"start": v(694.71, 429.16) * mm, "end": v(745.68, 417.56) * mm});
            skLineSegment(sketch, "E981", {"start": v(745.68, 417.56) * mm, "end": v(745.68, 408.27) * mm});
            skLineSegment(sketch, "E982", {"start": v(745.68, 408.27) * mm, "end": v(694.71, 398.54) * mm});
            skLineSegment(sketch, "E983", {"start": v(694.71, 398.54) * mm, "end": v(694.71, 429.16) * mm});
            skLineSegment(sketch, "E984", {"start": v(694.51, 651.68) * mm, "end": v(745.78, 640.14) * mm});
            skLineSegment(sketch, "E985", {"start": v(745.78, 640.14) * mm, "end": v(745.78, 630.92) * mm});
            skLineSegment(sketch, "E986", {"start": v(745.78, 630.92) * mm, "end": v(694.51, 620.95) * mm});
            skLineSegment(sketch, "E987", {"start": v(694.22, 869.02) * mm, "end": v(745.9, 857.52) * mm});
            skLineSegment(sketch, "E988", {"start": v(745.9, 857.52) * mm, "end": v(745.9, 848.23) * mm});
            skLineSegment(sketch, "E989", {"start": v(745.9, 848.23) * mm, "end": v(694.22, 838.06) * mm});
            skLineSegment(sketch, "E990", {"start": v(694.22, 838.06) * mm, "end": v(694.22, 869.02) * mm});
            skLineSegment(sketch, "E991", {"start": v(694.73, 1090.06) * mm, "end": v(745.84, 1078.67) * mm});
            skLineSegment(sketch, "E992", {"start": v(745.84, 1078.67) * mm, "end": v(745.84, 1069.35) * mm});
            skLineSegment(sketch, "E993", {"start": v(745.84, 1069.35) * mm, "end": v(694.73, 1059.4) * mm});
            skLineSegment(sketch, "E994", {"start": v(694.73, 1059.4) * mm, "end": v(694.73, 1090.06) * mm});
            skLineSegment(sketch, "E995", {"start": v(694.51, 651.68) * mm, "end": v(694.51, 620.95) * mm});
            skLineSegment(sketch, "E996", {"start": v(1054.59, 15.77) * mm, "end": v(1106, 4.62) * mm});
            skLineSegment(sketch, "E997", {"start": v(1106, 4.62) * mm, "end": v(1106, -5.12) * mm});
            skLineSegment(sketch, "E998", {"start": v(1106, -5.12) * mm, "end": v(1054.59, -14.85) * mm});
            skLineSegment(sketch, "E999", {"start": v(1054.59, -14.85) * mm, "end": v(1054.59, 15.77) * mm});
            skLineSegment(sketch, "E1000", {"start": v(1054.49, -398.5) * mm, "end": v(1054.49, -428.86) * mm});
            skLineSegment(sketch, "E1001", {"start": v(1054.49, -398.5) * mm, "end": v(1105.83, -409.81) * mm});
            skLineSegment(sketch, "E1002", {"start": v(1105.83, -409.81) * mm, "end": v(1105.83, -419.04) * mm});
            skLineSegment(sketch, "E1003", {"start": v(1105.83, -419.04) * mm, "end": v(1054.49, -428.86) * mm});
            skLineSegment(sketch, "E1004", {"start": v(1054.66, -187.78) * mm, "end": v(1105.78, -198.94) * mm});
            skLineSegment(sketch, "E1005", {"start": v(1105.78, -198.94) * mm, "end": v(1105.78, -208.53) * mm});
            skLineSegment(sketch, "E1006", {"start": v(1105.78, -208.53) * mm, "end": v(1054.59, -218.36) * mm});
            skLineSegment(sketch, "E1007", {"start": v(1054.59, -218.36) * mm, "end": v(1054.66, -187.78) * mm});
            skLineSegment(sketch, "E1008", {"start": v(1054.62, 221.38) * mm, "end": v(1105.88, 210.07) * mm});
            skLineSegment(sketch, "E1009", {"start": v(1105.88, 210.07) * mm, "end": v(1105.88, 200.47) * mm});
            skLineSegment(sketch, "E1010", {"start": v(1105.88, 200.47) * mm, "end": v(1054.54, 190.65) * mm});
            skLineSegment(sketch, "E1011", {"start": v(1054.54, 190.65) * mm, "end": v(1054.62, 221.38) * mm});
            skLineSegment(sketch, "E1012", {"start": v(1054.77, 429.16) * mm, "end": v(1105.74, 417.56) * mm});
            skLineSegment(sketch, "E1013", {"start": v(1105.74, 417.56) * mm, "end": v(1105.74, 408.27) * mm});
            skLineSegment(sketch, "E1014", {"start": v(1105.74, 408.27) * mm, "end": v(1054.77, 398.54) * mm});
            skLineSegment(sketch, "E1015", {"start": v(1054.77, 398.54) * mm, "end": v(1054.77, 429.16) * mm});
            skLineSegment(sketch, "E1016", {"start": v(1054.58, 651.68) * mm, "end": v(1105.84, 640.14) * mm});
            skLineSegment(sketch, "E1017", {"start": v(1105.84, 640.14) * mm, "end": v(1105.84, 630.92) * mm});
            skLineSegment(sketch, "E1018", {"start": v(1105.84, 630.92) * mm, "end": v(1054.58, 620.95) * mm});
            skLineSegment(sketch, "E1019", {"start": v(1054.28, 869.02) * mm, "end": v(1105.96, 857.52) * mm});
            skLineSegment(sketch, "E1020", {"start": v(1105.96, 857.52) * mm, "end": v(1105.96, 848.23) * mm});
            skLineSegment(sketch, "E1021", {"start": v(1105.96, 848.23) * mm, "end": v(1054.28, 838.06) * mm});
            skLineSegment(sketch, "E1022", {"start": v(1054.28, 838.06) * mm, "end": v(1054.28, 869.02) * mm});
            skLineSegment(sketch, "E1023", {"start": v(1054.79, 1090.06) * mm, "end": v(1105.9, 1078.67) * mm});
            skLineSegment(sketch, "E1024", {"start": v(1105.9, 1078.67) * mm, "end": v(1105.9, 1069.35) * mm});
            skLineSegment(sketch, "E1025", {"start": v(1105.9, 1069.35) * mm, "end": v(1054.79, 1059.4) * mm});
            skLineSegment(sketch, "E1026", {"start": v(1054.79, 1059.4) * mm, "end": v(1054.79, 1090.06) * mm});
            skLineSegment(sketch, "E1027", {"start": v(1054.58, 651.68) * mm, "end": v(1054.58, 620.95) * mm});
            skLineSegment(sketch, "E1028", {"start": v(1440.26, 15.94) * mm, "end": v(1491.67, 4.79) * mm});
            skLineSegment(sketch, "E1029", {"start": v(1491.67, 4.79) * mm, "end": v(1491.67, -4.95) * mm});
            skLineSegment(sketch, "E1030", {"start": v(1491.67, -4.95) * mm, "end": v(1440.26, -14.69) * mm});
            skLineSegment(sketch, "E1031", {"start": v(1440.26, -14.69) * mm, "end": v(1440.26, 15.94) * mm});
            skLineSegment(sketch, "E1032", {"start": v(1440.16, -398.33) * mm, "end": v(1440.16, -428.69) * mm});
            skLineSegment(sketch, "E1033", {"start": v(1440.16, -398.33) * mm, "end": v(1491.5, -409.64) * mm});
            skLineSegment(sketch, "E1034", {"start": v(1491.5, -409.64) * mm, "end": v(1491.5, -418.87) * mm});
            skLineSegment(sketch, "E1035", {"start": v(1491.5, -418.87) * mm, "end": v(1440.16, -428.69) * mm});
            skLineSegment(sketch, "E1036", {"start": v(1440.33, -187.6) * mm, "end": v(1491.45, -198.77) * mm});
            skLineSegment(sketch, "E1037", {"start": v(1491.45, -198.77) * mm, "end": v(1491.45, -208.37) * mm});
            skLineSegment(sketch, "E1038", {"start": v(1491.45, -208.37) * mm, "end": v(1440.26, -218.19) * mm});
            skLineSegment(sketch, "E1039", {"start": v(1440.26, -218.19) * mm, "end": v(1440.33, -187.6) * mm});
            skLineSegment(sketch, "E1040", {"start": v(1440.3, 221.55) * mm, "end": v(1491.56, 210.24) * mm});
            skLineSegment(sketch, "E1041", {"start": v(1491.56, 210.24) * mm, "end": v(1491.56, 200.64) * mm});
            skLineSegment(sketch, "E1042", {"start": v(1491.56, 200.64) * mm, "end": v(1440.22, 190.82) * mm});
            skLineSegment(sketch, "E1043", {"start": v(1440.22, 190.82) * mm, "end": v(1440.3, 221.55) * mm});
            skLineSegment(sketch, "E1044", {"start": v(1440.45, 429.32) * mm, "end": v(1491.41, 417.73) * mm});
            skLineSegment(sketch, "E1045", {"start": v(1491.41, 417.73) * mm, "end": v(1491.41, 408.44) * mm});
            skLineSegment(sketch, "E1046", {"start": v(1491.41, 408.44) * mm, "end": v(1440.45, 398.7) * mm});
            skLineSegment(sketch, "E1047", {"start": v(1440.45, 398.7) * mm, "end": v(1440.45, 429.32) * mm});
            skLineSegment(sketch, "E1048", {"start": v(1440.25, 651.84) * mm, "end": v(1491.51, 640.31) * mm});
            skLineSegment(sketch, "E1049", {"start": v(1491.51, 640.31) * mm, "end": v(1491.51, 631.09) * mm});
            skLineSegment(sketch, "E1050", {"start": v(1491.51, 631.09) * mm, "end": v(1440.25, 621.12) * mm});
            skLineSegment(sketch, "E1051", {"start": v(1439.95, 869.2) * mm, "end": v(1491.63, 857.7) * mm});
            skLineSegment(sketch, "E1052", {"start": v(1491.63, 857.7) * mm, "end": v(1491.63, 848.4) * mm});
            skLineSegment(sketch, "E1053", {"start": v(1491.63, 848.4) * mm, "end": v(1439.95, 838.22) * mm});
            skLineSegment(sketch, "E1054", {"start": v(1439.95, 838.22) * mm, "end": v(1439.95, 869.2) * mm});
            skLineSegment(sketch, "E1055", {"start": v(1440.46, 1090.23) * mm, "end": v(1491.58, 1078.84) * mm});
            skLineSegment(sketch, "E1056", {"start": v(1491.58, 1078.84) * mm, "end": v(1491.58, 1069.52) * mm});
            skLineSegment(sketch, "E1057", {"start": v(1491.58, 1069.52) * mm, "end": v(1440.46, 1059.57) * mm});
            skLineSegment(sketch, "E1058", {"start": v(1440.46, 1059.57) * mm, "end": v(1440.46, 1090.23) * mm});
            skLineSegment(sketch, "E1059", {"start": v(1440.25, 651.84) * mm, "end": v(1440.25, 621.12) * mm});
            skLineSegment(sketch, "E1060", {"start": v(1800.32, 15.94) * mm, "end": v(1851.74, 4.79) * mm});
            skLineSegment(sketch, "E1061", {"start": v(1851.74, 4.79) * mm, "end": v(1851.74, -4.95) * mm});
            skLineSegment(sketch, "E1062", {"start": v(1851.74, -4.95) * mm, "end": v(1800.32, -14.69) * mm});
            skLineSegment(sketch, "E1063", {"start": v(1800.32, -14.69) * mm, "end": v(1800.32, 15.94) * mm});
            skLineSegment(sketch, "E1064", {"start": v(1800.22, -398.33) * mm, "end": v(1800.22, -428.69) * mm});
            skLineSegment(sketch, "E1065", {"start": v(1800.22, -398.33) * mm, "end": v(1851.56, -409.64) * mm});
            skLineSegment(sketch, "E1066", {"start": v(1851.56, -409.64) * mm, "end": v(1851.56, -418.87) * mm});
            skLineSegment(sketch, "E1067", {"start": v(1851.56, -418.87) * mm, "end": v(1800.22, -428.69) * mm});
            skLineSegment(sketch, "E1068", {"start": v(1800.4, -187.6) * mm, "end": v(1851.51, -198.77) * mm});
            skLineSegment(sketch, "E1069", {"start": v(1851.51, -198.77) * mm, "end": v(1851.51, -208.37) * mm});
            skLineSegment(sketch, "E1070", {"start": v(1851.51, -208.37) * mm, "end": v(1800.32, -218.19) * mm});
            skLineSegment(sketch, "E1071", {"start": v(1800.32, -218.19) * mm, "end": v(1800.4, -187.6) * mm});
            skLineSegment(sketch, "E1072", {"start": v(1800.35, 221.55) * mm, "end": v(1851.62, 210.24) * mm});
            skLineSegment(sketch, "E1073", {"start": v(1851.62, 210.24) * mm, "end": v(1851.62, 200.64) * mm});
            skLineSegment(sketch, "E1074", {"start": v(1851.62, 200.64) * mm, "end": v(1800.28, 190.82) * mm});
            skLineSegment(sketch, "E1075", {"start": v(1800.28, 190.82) * mm, "end": v(1800.35, 221.55) * mm});
            skLineSegment(sketch, "E1076", {"start": v(1800.5, 429.32) * mm, "end": v(1851.47, 417.73) * mm});
            skLineSegment(sketch, "E1077", {"start": v(1851.47, 417.73) * mm, "end": v(1851.47, 408.44) * mm});
            skLineSegment(sketch, "E1078", {"start": v(1851.47, 408.44) * mm, "end": v(1800.5, 398.7) * mm});
            skLineSegment(sketch, "E1079", {"start": v(1800.5, 398.7) * mm, "end": v(1800.5, 429.32) * mm});
            skLineSegment(sketch, "E1080", {"start": v(1800.3, 651.84) * mm, "end": v(1851.57, 640.31) * mm});
            skLineSegment(sketch, "E1081", {"start": v(1851.57, 640.31) * mm, "end": v(1851.57, 631.09) * mm});
            skLineSegment(sketch, "E1082", {"start": v(1851.57, 631.09) * mm, "end": v(1800.3, 621.12) * mm});
            skLineSegment(sketch, "E1083", {"start": v(1800.02, 869.2) * mm, "end": v(1851.69, 857.7) * mm});
            skLineSegment(sketch, "E1084", {"start": v(1851.69, 857.7) * mm, "end": v(1851.69, 848.4) * mm});
            skLineSegment(sketch, "E1085", {"start": v(1851.69, 848.4) * mm, "end": v(1800.02, 838.22) * mm});
            skLineSegment(sketch, "E1086", {"start": v(1800.02, 838.22) * mm, "end": v(1800.02, 869.2) * mm});
            skLineSegment(sketch, "E1087", {"start": v(1800.52, 1090.23) * mm, "end": v(1851.64, 1078.84) * mm});
            skLineSegment(sketch, "E1088", {"start": v(1851.64, 1078.84) * mm, "end": v(1851.64, 1069.52) * mm});
            skLineSegment(sketch, "E1089", {"start": v(1851.64, 1069.52) * mm, "end": v(1800.52, 1059.57) * mm});
            skLineSegment(sketch, "E1090", {"start": v(1800.52, 1059.57) * mm, "end": v(1800.52, 1090.23) * mm});
            skLineSegment(sketch, "E1091", {"start": v(1800.3, 651.84) * mm, "end": v(1800.3, 621.12) * mm});
            skLineSegment(sketch, "E1092", {"start": v(2186.2, 15.69) * mm, "end": v(2237.61, 4.53) * mm});
            skLineSegment(sketch, "E1093", {"start": v(2237.61, 4.53) * mm, "end": v(2237.61, -5.2) * mm});
            skLineSegment(sketch, "E1094", {"start": v(2237.61, -5.2) * mm, "end": v(2186.2, -14.94) * mm});
            skLineSegment(sketch, "E1095", {"start": v(2186.2, -14.94) * mm, "end": v(2186.2, 15.69) * mm});
            skLineSegment(sketch, "E1096", {"start": v(2186.1, -398.58) * mm, "end": v(2186.1, -428.94) * mm});
            skLineSegment(sketch, "E1097", {"start": v(2186.1, -398.58) * mm, "end": v(2237.44, -409.9) * mm});
            skLineSegment(sketch, "E1098", {"start": v(2237.44, -409.9) * mm, "end": v(2237.44, -419.12) * mm});
            skLineSegment(sketch, "E1099", {"start": v(2237.44, -419.12) * mm, "end": v(2186.1, -428.94) * mm});
            skLineSegment(sketch, "E1100", {"start": v(2186.27, -187.86) * mm, "end": v(2237.39, -199.02) * mm});
            skLineSegment(sketch, "E1101", {"start": v(2237.39, -199.02) * mm, "end": v(2237.39, -208.62) * mm});
            skLineSegment(sketch, "E1102", {"start": v(2237.39, -208.62) * mm, "end": v(2186.2, -218.44) * mm});
            skLineSegment(sketch, "E1103", {"start": v(2186.2, -218.44) * mm, "end": v(2186.27, -187.86) * mm});
            skLineSegment(sketch, "E1104", {"start": v(2186.23, 221.3) * mm, "end": v(2237.5, 209.99) * mm});
            skLineSegment(sketch, "E1105", {"start": v(2237.5, 209.99) * mm, "end": v(2237.5, 200.39) * mm});
            skLineSegment(sketch, "E1106", {"start": v(2237.5, 200.39) * mm, "end": v(2186.16, 190.57) * mm});
            skLineSegment(sketch, "E1107", {"start": v(2186.16, 190.57) * mm, "end": v(2186.23, 221.3) * mm});
            skLineSegment(sketch, "E1108", {"start": v(2186.39, 429.07) * mm, "end": v(2237.35, 417.48) * mm});
            skLineSegment(sketch, "E1109", {"start": v(2237.35, 417.48) * mm, "end": v(2237.35, 408.2) * mm});
            skLineSegment(sketch, "E1110", {"start": v(2237.35, 408.2) * mm, "end": v(2186.39, 398.46) * mm});
            skLineSegment(sketch, "E1111", {"start": v(2186.39, 398.46) * mm, "end": v(2186.39, 429.07) * mm});
            skLineSegment(sketch, "E1112", {"start": v(2186.19, 651.6) * mm, "end": v(2237.45, 640.06) * mm});
            skLineSegment(sketch, "E1113", {"start": v(2237.45, 640.06) * mm, "end": v(2237.45, 630.83) * mm});
            skLineSegment(sketch, "E1114", {"start": v(2237.45, 630.83) * mm, "end": v(2186.19, 620.86) * mm});
            skLineSegment(sketch, "E1115", {"start": v(2185.9, 868.94) * mm, "end": v(2237.57, 857.44) * mm});
            skLineSegment(sketch, "E1116", {"start": v(2237.57, 857.44) * mm, "end": v(2237.57, 848.15) * mm});
            skLineSegment(sketch, "E1117", {"start": v(2237.57, 848.15) * mm, "end": v(2185.9, 837.97) * mm});
            skLineSegment(sketch, "E1118", {"start": v(2185.9, 837.97) * mm, "end": v(2185.9, 868.94) * mm});
            skLineSegment(sketch, "E1119", {"start": v(2186.4, 1089.98) * mm, "end": v(2237.52, 1078.6) * mm});
            skLineSegment(sketch, "E1120", {"start": v(2237.52, 1078.6) * mm, "end": v(2237.52, 1069.27) * mm});
            skLineSegment(sketch, "E1121", {"start": v(2237.52, 1069.27) * mm, "end": v(2186.4, 1059.32) * mm});
            skLineSegment(sketch, "E1122", {"start": v(2186.4, 1059.32) * mm, "end": v(2186.4, 1089.98) * mm});
            skLineSegment(sketch, "E1123", {"start": v(2186.19, 651.6) * mm, "end": v(2186.19, 620.86) * mm});
            skLineSegment(sketch, "E1124", {"start": v(2546.26, 15.69) * mm, "end": v(2597.68, 4.53) * mm});
            skLineSegment(sketch, "E1125", {"start": v(2597.68, 4.53) * mm, "end": v(2597.68, -5.2) * mm});
            skLineSegment(sketch, "E1126", {"start": v(2597.68, -5.2) * mm, "end": v(2546.26, -14.94) * mm});
            skLineSegment(sketch, "E1127", {"start": v(2546.26, -14.94) * mm, "end": v(2546.26, 15.69) * mm});
            skLineSegment(sketch, "E1128", {"start": v(2546.16, -398.58) * mm, "end": v(2546.16, -428.94) * mm});
            skLineSegment(sketch, "E1129", {"start": v(2546.16, -398.58) * mm, "end": v(2597.5, -409.9) * mm});
            skLineSegment(sketch, "E1130", {"start": v(2597.5, -409.9) * mm, "end": v(2597.5, -419.12) * mm});
            skLineSegment(sketch, "E1131", {"start": v(2597.5, -419.12) * mm, "end": v(2546.16, -428.94) * mm});
            skLineSegment(sketch, "E1132", {"start": v(2546.34, -187.86) * mm, "end": v(2597.45, -199.02) * mm});
            skLineSegment(sketch, "E1133", {"start": v(2597.45, -199.02) * mm, "end": v(2597.45, -208.62) * mm});
            skLineSegment(sketch, "E1134", {"start": v(2597.45, -208.62) * mm, "end": v(2546.26, -218.44) * mm});
            skLineSegment(sketch, "E1135", {"start": v(2546.26, -218.44) * mm, "end": v(2546.34, -187.86) * mm});
            skLineSegment(sketch, "E1136", {"start": v(2546.3, 221.3) * mm, "end": v(2597.56, 209.99) * mm});
            skLineSegment(sketch, "E1137", {"start": v(2597.56, 209.99) * mm, "end": v(2597.56, 200.39) * mm});
            skLineSegment(sketch, "E1138", {"start": v(2597.56, 200.39) * mm, "end": v(2546.22, 190.57) * mm});
            skLineSegment(sketch, "E1139", {"start": v(2546.22, 190.57) * mm, "end": v(2546.3, 221.3) * mm});
            skLineSegment(sketch, "E1140", {"start": v(2546.45, 429.07) * mm, "end": v(2597.41, 417.48) * mm});
            skLineSegment(sketch, "E1141", {"start": v(2597.41, 417.48) * mm, "end": v(2597.41, 408.2) * mm});
            skLineSegment(sketch, "E1142", {"start": v(2597.41, 408.2) * mm, "end": v(2546.45, 398.46) * mm});
            skLineSegment(sketch, "E1143", {"start": v(2546.45, 398.46) * mm, "end": v(2546.45, 429.07) * mm});
            skLineSegment(sketch, "E1144", {"start": v(2546.25, 651.6) * mm, "end": v(2597.51, 640.06) * mm});
            skLineSegment(sketch, "E1145", {"start": v(2597.51, 640.06) * mm, "end": v(2597.51, 630.83) * mm});
            skLineSegment(sketch, "E1146", {"start": v(2597.51, 630.83) * mm, "end": v(2546.25, 620.86) * mm});
            skLineSegment(sketch, "E1147", {"start": v(2545.96, 868.94) * mm, "end": v(2597.63, 857.44) * mm});
            skLineSegment(sketch, "E1148", {"start": v(2597.63, 857.44) * mm, "end": v(2597.63, 848.15) * mm});
            skLineSegment(sketch, "E1149", {"start": v(2597.63, 848.15) * mm, "end": v(2545.96, 837.97) * mm});
            skLineSegment(sketch, "E1150", {"start": v(2545.96, 837.97) * mm, "end": v(2545.96, 868.94) * mm});
            skLineSegment(sketch, "E1151", {"start": v(2546.46, 1089.98) * mm, "end": v(2597.58, 1078.6) * mm});
            skLineSegment(sketch, "E1152", {"start": v(2597.58, 1078.6) * mm, "end": v(2597.58, 1069.27) * mm});
            skLineSegment(sketch, "E1153", {"start": v(2597.58, 1069.27) * mm, "end": v(2546.46, 1059.32) * mm});
            skLineSegment(sketch, "E1154", {"start": v(2546.46, 1059.32) * mm, "end": v(2546.46, 1089.98) * mm});
            skLineSegment(sketch, "E1155", {"start": v(2546.25, 651.6) * mm, "end": v(2546.25, 620.86) * mm});
            skSolve(sketch);
        }
        {
            var Q0;
            Q0=qSketchRegion(id+"F6",true);
            extrude(context, id + "F7", {"entities" : qUnion([Q0]), "depth" : 7.62 * mm, "offsetDistance" : 25.4 * mm});
        }
        {
            var Q0;
            Q0=makeQuery(id+"F1.opExtrude","CAP_FACE",FACE,{"disambiguationData":[OSD([sQuery(id+"F0.wireOp",EDGE,"E0.left"),sQuery(id+"F0.wireOp",EDGE,"E1"),sQuery(id+"F0.wireOp",EDGE,"E2"),sQuery(id+"F0.wireOp",EDGE,"E3")])],"isStart":true});
            var sketch = newSketch(context, id + "F8", { "sketchPlane" : qUnion([Q0])});
            skLineSegment(sketch, "E1156.top", {"start": v(-260.05, -574.1) * mm, "end": v(-229.56, -574.1) * mm});
            skLineSegment(sketch, "E1156.left", {"start": v(-260.05, 1249.82) * mm, "end": v(-260.05, -574.1) * mm});
            skLineSegment(sketch, "E1156.right", {"start": v(-229.56, 1249.82) * mm, "end": v(-229.56, -574.1) * mm});
            skArc(sketch, "E1157", {"start": v(-260.05, 1249.82) * mm, "mid": v(-266.07, 1264.17) * mm, "end": v(-280.52, 1269.96) * mm});
            skArc(sketch, "E1158", {"start": v(-229.56, 1249.82) * mm, "mid": v(-244.14, 1285.52) * mm, "end": v(-279.54, 1300.83) * mm});
            skLineSegment(sketch, "E1159", {"start": v(-280.52, 1269.96) * mm, "end": v(-407.01, 1269.96) * mm});
            skLineSegment(sketch, "E1160", {"start": v(-407.01, 1269.96) * mm, "end": v(-407.01, 1300.83) * mm});
            skLineSegment(sketch, "E1161", {"start": v(-279.54, 1300.83) * mm, "end": v(-407.01, 1300.83) * mm});
            skLineSegment(sketch, "E1162.top", {"start": v(95.2, -574.1) * mm, "end": v(125.69, -574.1) * mm});
            skLineSegment(sketch, "E1162.left", {"start": v(95.2, 1249.82) * mm, "end": v(95.2, -574.1) * mm});
            skLineSegment(sketch, "E1162.right", {"start": v(125.69, 1249.82) * mm, "end": v(125.69, -574.1) * mm});
            skArc(sketch, "E1163", {"start": v(95.2, 1249.82) * mm, "mid": v(89.18, 1264.17) * mm, "end": v(74.74, 1269.96) * mm});
            skArc(sketch, "E1164", {"start": v(125.69, 1249.82) * mm, "mid": v(111.11, 1285.52) * mm, "end": v(75.72, 1300.83) * mm});
            skLineSegment(sketch, "E1165", {"start": v(74.74, 1269.96) * mm, "end": v(-51.76, 1269.96) * mm});
            skLineSegment(sketch, "E1166", {"start": v(-51.76, 1269.96) * mm, "end": v(-51.76, 1300.83) * mm});
            skLineSegment(sketch, "E1167", {"start": v(75.72, 1300.83) * mm, "end": v(-51.76, 1300.83) * mm});
            skLineSegment(sketch, "E1168.top", {"start": v(486, -574.1) * mm, "end": v(516.5, -574.1) * mm});
            skLineSegment(sketch, "E1168.left", {"start": v(486, 1249.82) * mm, "end": v(486, -574.1) * mm});
            skLineSegment(sketch, "E1168.right", {"start": v(516.5, 1249.82) * mm, "end": v(516.5, -574.1) * mm});
            skArc(sketch, "E1169", {"start": v(486, 1249.82) * mm, "mid": v(480, 1264.17) * mm, "end": v(465.55, 1269.96) * mm});
            skArc(sketch, "E1170", {"start": v(516.5, 1249.82) * mm, "mid": v(501.92, 1285.52) * mm, "end": v(466.53, 1300.83) * mm});
            skLineSegment(sketch, "E1171", {"start": v(465.55, 1269.96) * mm, "end": v(339.05, 1269.96) * mm});
            skLineSegment(sketch, "E1172", {"start": v(339.05, 1269.96) * mm, "end": v(339.05, 1300.83) * mm});
            skLineSegment(sketch, "E1173", {"start": v(466.53, 1300.83) * mm, "end": v(339.05, 1300.83) * mm});
            skLineSegment(sketch, "E1174.top", {"start": v(841.26, -574.1) * mm, "end": v(871.75, -574.1) * mm});
            skLineSegment(sketch, "E1174.left", {"start": v(841.26, 1249.82) * mm, "end": v(841.26, -574.1) * mm});
            skLineSegment(sketch, "E1174.right", {"start": v(871.75, 1249.82) * mm, "end": v(871.75, -574.1) * mm});
            skArc(sketch, "E1175", {"start": v(841.26, 1249.82) * mm, "mid": v(835.25, 1264.17) * mm, "end": v(820.8, 1269.96) * mm});
            skArc(sketch, "E1176", {"start": v(871.75, 1249.82) * mm, "mid": v(857.18, 1285.52) * mm, "end": v(821.78, 1300.83) * mm});
            skLineSegment(sketch, "E1177", {"start": v(820.8, 1269.96) * mm, "end": v(694.3, 1269.96) * mm});
            skLineSegment(sketch, "E1178", {"start": v(694.3, 1269.96) * mm, "end": v(694.3, 1300.83) * mm});
            skLineSegment(sketch, "E1179", {"start": v(821.78, 1300.83) * mm, "end": v(694.3, 1300.83) * mm});
            skLineSegment(sketch, "E1180.top", {"start": v(1224.81, -574.1) * mm, "end": v(1255.3, -574.1) * mm});
            skLineSegment(sketch, "E1180.left", {"start": v(1224.81, 1249.82) * mm, "end": v(1224.81, -574.1) * mm});
            skLineSegment(sketch, "E1180.right", {"start": v(1255.3, 1249.82) * mm, "end": v(1255.3, -574.1) * mm});
            skArc(sketch, "E1181", {"start": v(1224.81, 1249.82) * mm, "mid": v(1218.8, 1264.17) * mm, "end": v(1204.35, 1269.96) * mm});
            skArc(sketch, "E1182", {"start": v(1255.3, 1249.82) * mm, "mid": v(1240.73, 1285.52) * mm, "end": v(1205.33, 1300.83) * mm});
            skLineSegment(sketch, "E1183", {"start": v(1204.35, 1269.96) * mm, "end": v(1077.85, 1269.96) * mm});
            skLineSegment(sketch, "E1184", {"start": v(1077.85, 1269.96) * mm, "end": v(1077.85, 1300.83) * mm});
            skLineSegment(sketch, "E1185", {"start": v(1205.33, 1300.83) * mm, "end": v(1077.85, 1300.83) * mm});
            skLineSegment(sketch, "E1186.top", {"start": v(1580.06, -574.1) * mm, "end": v(1610.55, -574.1) * mm});
            skLineSegment(sketch, "E1186.left", {"start": v(1580.06, 1249.82) * mm, "end": v(1580.06, -574.1) * mm});
            skLineSegment(sketch, "E1186.right", {"start": v(1610.55, 1249.82) * mm, "end": v(1610.55, -574.1) * mm});
            skArc(sketch, "E1187", {"start": v(1580.06, 1249.82) * mm, "mid": v(1574.05, 1264.17) * mm, "end": v(1559.6, 1269.96) * mm});
            skArc(sketch, "E1188", {"start": v(1610.55, 1249.82) * mm, "mid": v(1595.98, 1285.52) * mm, "end": v(1560.58, 1300.83) * mm});
            skLineSegment(sketch, "E1189", {"start": v(1559.6, 1269.96) * mm, "end": v(1433.1, 1269.96) * mm});
            skLineSegment(sketch, "E1190", {"start": v(1433.1, 1269.96) * mm, "end": v(1433.1, 1300.83) * mm});
            skLineSegment(sketch, "E1191", {"start": v(1560.58, 1300.83) * mm, "end": v(1433.1, 1300.83) * mm});
            skLineSegment(sketch, "E1192.top", {"start": v(1970.87, -574.1) * mm, "end": v(2001.36, -574.1) * mm});
            skLineSegment(sketch, "E1192.left", {"start": v(1970.87, 1249.82) * mm, "end": v(1970.87, -574.1) * mm});
            skLineSegment(sketch, "E1192.right", {"start": v(2001.36, 1249.82) * mm, "end": v(2001.36, -574.1) * mm});
            skArc(sketch, "E1193", {"start": v(1970.87, 1249.82) * mm, "mid": v(1964.86, 1264.17) * mm, "end": v(1950.41, 1269.96) * mm});
            skArc(sketch, "E1194", {"start": v(2001.36, 1249.82) * mm, "mid": v(1986.79, 1285.52) * mm, "end": v(1951.4, 1300.83) * mm});
            skLineSegment(sketch, "E1195", {"start": v(1950.41, 1269.96) * mm, "end": v(1823.91, 1269.96) * mm});
            skLineSegment(sketch, "E1196", {"start": v(1823.91, 1269.96) * mm, "end": v(1823.91, 1300.83) * mm});
            skLineSegment(sketch, "E1197", {"start": v(1951.4, 1300.83) * mm, "end": v(1823.91, 1300.83) * mm});
            skLineSegment(sketch, "E1198.top", {"start": v(2326.12, -574.1) * mm, "end": v(2356.61, -574.1) * mm});
            skLineSegment(sketch, "E1198.left", {"start": v(2326.12, 1249.82) * mm, "end": v(2326.12, -574.1) * mm});
            skLineSegment(sketch, "E1198.right", {"start": v(2356.61, 1249.82) * mm, "end": v(2356.61, -574.1) * mm});
            skArc(sketch, "E1199", {"start": v(2326.12, 1249.82) * mm, "mid": v(2320.11, 1264.17) * mm, "end": v(2305.66, 1269.96) * mm});
            skArc(sketch, "E1200", {"start": v(2356.61, 1249.82) * mm, "mid": v(2342.04, 1285.52) * mm, "end": v(2306.64, 1300.83) * mm});
            skLineSegment(sketch, "E1201", {"start": v(2305.66, 1269.96) * mm, "end": v(2179.16, 1269.96) * mm});
            skLineSegment(sketch, "E1202", {"start": v(2179.16, 1269.96) * mm, "end": v(2179.16, 1300.83) * mm});
            skLineSegment(sketch, "E1203", {"start": v(2306.64, 1300.83) * mm, "end": v(2179.16, 1300.83) * mm});
            skPoint(sketch, "E1204.oppositeSnap0", {"position": v(1496.35, 1269.96) * mm});
            skLineSegment(sketch, "E1204.bottom", {"start": v(-932.57, 1356.55) * mm, "end": v(2710.02, 1356.55) * mm});
            skLineSegment(sketch, "E1204.top", {"start": v(-932.57, 1324.69) * mm, "end": v(2710.02, 1324.69) * mm});
            skLineSegment(sketch, "E1204.left", {"start": v(-932.57, 1356.55) * mm, "end": v(-932.57, 1324.69) * mm});
            skLineSegment(sketch, "E1204.right", {"start": v(2710.02, 1356.55) * mm, "end": v(2710.02, 1324.69) * mm});
            skLineSegment(sketch, "E1205.top", {"start": v(-574.34, 1269.12) * mm, "end": v(-711.4, 1269.12) * mm});
            skLineSegment(sketch, "E1205.left", {"start": v(-574.34, 1297.98) * mm, "end": v(-574.34, 1269.12) * mm});
            skLineSegment(sketch, "E1206", {"start": v(-574.34, 1297.98) * mm, "end": v(-711.4, 1297.98) * mm});
            skArc(sketch, "E1207", {"start": v(-711.4, 1297.98) * mm, "mid": v(-731.13, 1290.25) * mm, "end": v(-740.37, 1271.18) * mm});
            skLineSegment(sketch, "E1208", {"start": v(-740.37, 1271.18) * mm, "end": v(-740.37, 1242.75) * mm});
            skLineSegment(sketch, "E1209", {"start": v(-740.37, 1242.75) * mm, "end": v(-930.97, 1242.75) * mm});
            skLineSegment(sketch, "E1210", {"start": v(-930.97, 1214.96) * mm, "end": v(-930.97, 1242.75) * mm});
            skLineSegment(sketch, "E1211", {"start": v(-711.4, 1269.12) * mm, "end": v(-711.4, 1242.75) * mm});
            skLineSegment(sketch, "E1212", {"start": v(-930.97, 1214.96) * mm, "end": v(-740.37, 1214.96) * mm});
            skArc(sketch, "E1213", {"start": v(-711.4, 1242.75) * mm, "mid": v(-719.96, 1222.68) * mm, "end": v(-740.37, 1214.96) * mm});
            skSolve(sketch);
        }
        {
            var Q0;
            Q0 = qSketchRegion(id + "F8", true);
            extrude(context, id + "F9", {"entities" : qUnion([Q0]), "depth" : 10.16 * mm, "offsetDistance" : 25.4 * mm});
        }
    });
